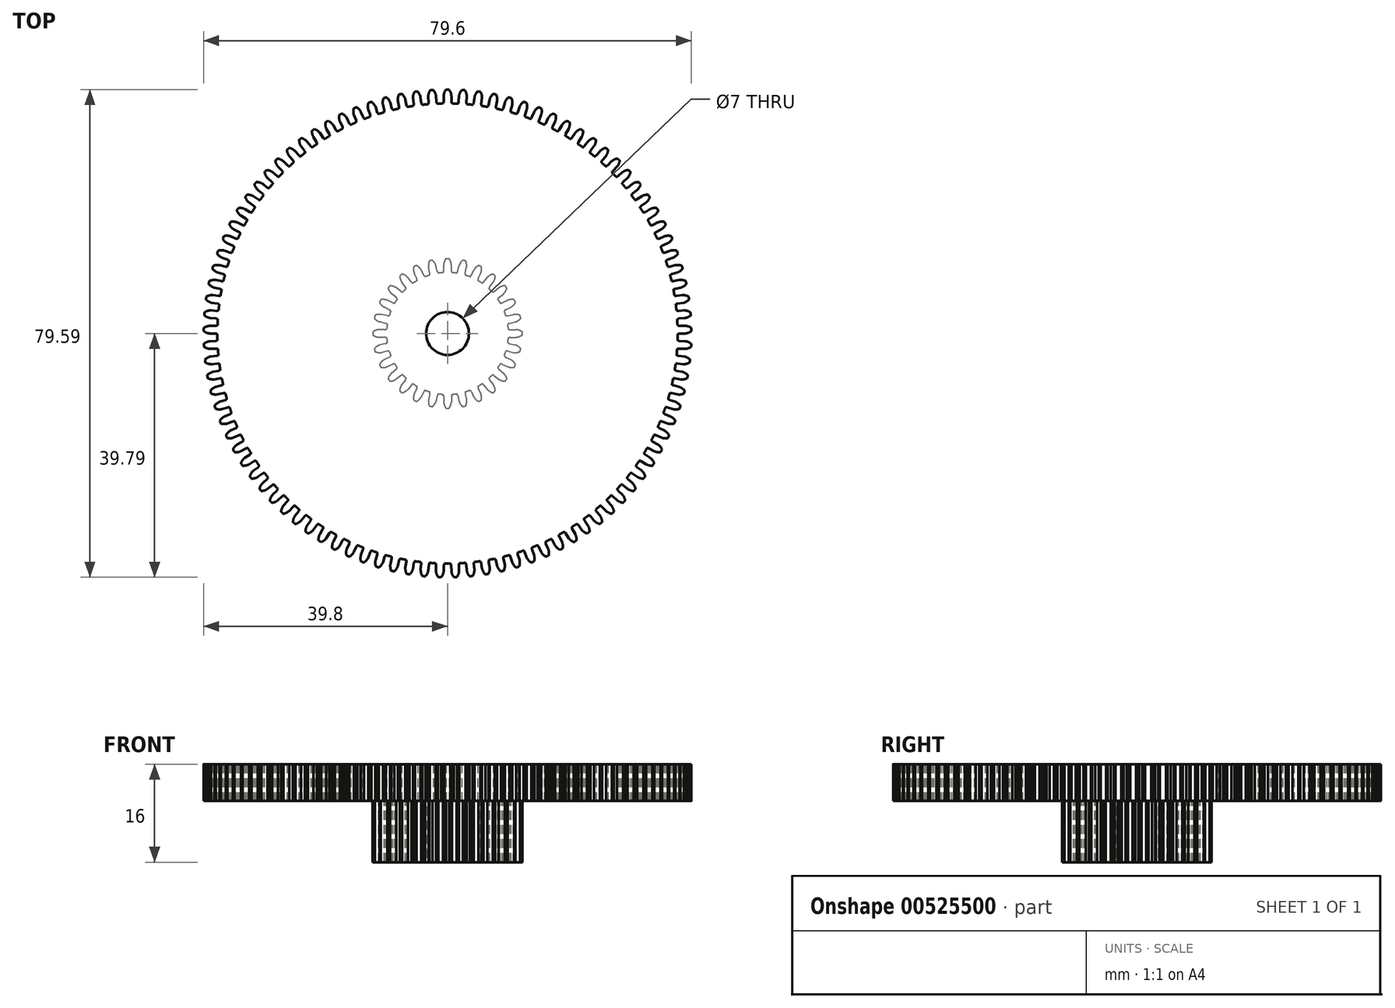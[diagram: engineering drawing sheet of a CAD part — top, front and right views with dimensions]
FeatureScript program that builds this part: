
annotation { "Feature Type Name" : "Feature", "Feature Type Description" : "" }
export const myFeature = defineFeature(function(context is Context, id is Id, definition is map)
    precondition{}
    {
        {
            var Q0;
            Q0=qCreatedBy(makeId("Top.planeOp"),FACE);
            var sketch = newSketch(context, id + "F0", { "sketchPlane" : qUnion([Q0])});
            skCircle(sketch, "E0", {"center": v(0, 0) * mm, "radius": 37.55 * mm, "construction": true});
            skCircle(sketch, "E1", {"center": v(0, 0) * mm, "radius": 38.8 * mm, "construction": true});
            skArc(sketch, "E2", {"start": v(0.25, 39.8) * mm, "mid": v(0, 39.8) * mm, "end": v(-0.25, 39.8) * mm});
            skLineSegment(sketch, "E3", {"start": v(-0.63, 39.8) * mm, "end": v(-0.63, 37.54) * mm, "construction": true});
            skLineSegment(sketch, "E4", {"start": v(0.63, 37.54) * mm, "end": v(0.63, 39.8) * mm, "construction": true});
            skArc(sketch, "E5", {"start": v(-0.25, 39.8) * mm, "mid": v(-0.5, 39.32) * mm, "end": v(-0.63, 38.8) * mm});
            skArc(sketch, "E6", {"start": v(-0.73, 37.54) * mm, "mid": v(-0.67, 37.69) * mm, "end": v(-0.63, 37.84) * mm});
            skLineSegment(sketch, "E7", {"start": v(-0.63, 37.84) * mm, "end": v(-0.63, 38.8) * mm});
            skArc(sketch, "E8.MirrorCS", {"start": v(0.25, 39.8) * mm, "mid": v(0.5, 39.32) * mm, "end": v(0.63, 38.8) * mm});
            skLineSegment(sketch, "E9.MirrorCS", {"start": v(0.63, 37.84) * mm, "end": v(0.63, 38.8) * mm});
            skArc(sketch, "E10.MirrorCS", {"start": v(0.73, 37.54) * mm, "mid": v(0.67, 37.69) * mm, "end": v(0.63, 37.84) * mm});
            skArc(sketch, "E11.1.0", {"start": v(-3.16, 37.42) * mm, "mid": v(-3.1, 37.57) * mm, "end": v(-3.08, 37.72) * mm});
            skLineSegment(sketch, "E11.1.1", {"start": v(-3.08, 37.72) * mm, "end": v(-3.14, 38.67) * mm});
            skArc(sketch, "E11.1.2", {"start": v(-2.83, 39.7) * mm, "mid": v(-3.05, 39.2) * mm, "end": v(-3.14, 38.67) * mm});
            skArc(sketch, "E11.1.3", {"start": v(-2.33, 39.73) * mm, "mid": v(-2.58, 39.72) * mm, "end": v(-2.83, 39.7) * mm});
            skArc(sketch, "E11.1.4", {"start": v(-2.33, 39.73) * mm, "mid": v(-2.04, 39.27) * mm, "end": v(-1.88, 38.75) * mm});
            skLineSegment(sketch, "E11.1.5", {"start": v(-1.82, 37.8) * mm, "end": v(-1.88, 38.75) * mm});
            skArc(sketch, "E11.1.6", {"start": v(-1.7, 37.51) * mm, "mid": v(-1.77, 37.65) * mm, "end": v(-1.82, 37.8) * mm});
            skArc(sketch, "E11.2.0", {"start": v(-5.57, 37.13) * mm, "mid": v(-5.53, 37.29) * mm, "end": v(-5.51, 37.45) * mm});
            skLineSegment(sketch, "E11.2.1", {"start": v(-5.51, 37.45) * mm, "end": v(-5.63, 38.39) * mm});
            skArc(sketch, "E11.2.2", {"start": v(-5.39, 39.43) * mm, "mid": v(-5.58, 38.93) * mm, "end": v(-5.63, 38.39) * mm});
            skArc(sketch, "E11.2.3", {"start": v(-4.9, 39.5) * mm, "mid": v(-5.14, 39.47) * mm, "end": v(-5.39, 39.43) * mm});
            skArc(sketch, "E11.2.4", {"start": v(-4.9, 39.5) * mm, "mid": v(-4.58, 39.06) * mm, "end": v(-4.39, 38.55) * mm});
            skLineSegment(sketch, "E11.2.5", {"start": v(-4.27, 37.6) * mm, "end": v(-4.39, 38.55) * mm});
            skArc(sketch, "E11.2.6", {"start": v(-4.13, 37.32) * mm, "mid": v(-4.2, 37.46) * mm, "end": v(-4.27, 37.6) * mm});
            skArc(sketch, "E11.3.0", {"start": v(-7.96, 36.7) * mm, "mid": v(-7.93, 36.85) * mm, "end": v(-7.92, 37.01) * mm});
            skLineSegment(sketch, "E11.3.1", {"start": v(-7.92, 37.01) * mm, "end": v(-8.1, 37.94) * mm});
            skArc(sketch, "E11.3.2", {"start": v(-7.93, 39) * mm, "mid": v(-8.1, 38.48) * mm, "end": v(-8.1, 37.94) * mm});
            skArc(sketch, "E11.3.3", {"start": v(-7.44, 39.1) * mm, "mid": v(-7.69, 39.05) * mm, "end": v(-7.93, 39) * mm});
            skArc(sketch, "E11.3.4", {"start": v(-7.44, 39.1) * mm, "mid": v(-7.1, 38.68) * mm, "end": v(-6.87, 38.19) * mm});
            skLineSegment(sketch, "E11.3.5", {"start": v(-6.7, 37.25) * mm, "end": v(-6.87, 38.19) * mm});
            skArc(sketch, "E11.3.6", {"start": v(-6.54, 36.98) * mm, "mid": v(-6.62, 37.1) * mm, "end": v(-6.7, 37.25) * mm});
            skArc(sketch, "E11.4.0", {"start": v(-10.32, 36.1) * mm, "mid": v(-10.3, 36.26) * mm, "end": v(-10.3, 36.42) * mm});
            skLineSegment(sketch, "E11.4.1", {"start": v(-10.3, 36.42) * mm, "end": v(-10.55, 37.34) * mm});
            skArc(sketch, "E11.4.2", {"start": v(-10.44, 38.4) * mm, "mid": v(-10.57, 37.88) * mm, "end": v(-10.55, 37.34) * mm});
            skArc(sketch, "E11.4.3", {"start": v(-9.96, 38.53) * mm, "mid": v(-10.2, 38.47) * mm, "end": v(-10.44, 38.4) * mm});
            skArc(sketch, "E11.4.4", {"start": v(-9.96, 38.53) * mm, "mid": v(-9.58, 38.14) * mm, "end": v(-9.33, 37.66) * mm});
            skLineSegment(sketch, "E11.4.5", {"start": v(-9.09, 36.74) * mm, "end": v(-9.33, 37.66) * mm});
            skArc(sketch, "E11.4.6", {"start": v(-8.91, 36.48) * mm, "mid": v(-9.01, 36.6) * mm, "end": v(-9.09, 36.74) * mm});
            skArc(sketch, "E11.5.0", {"start": v(-12.64, 35.36) * mm, "mid": v(-12.63, 35.52) * mm, "end": v(-12.64, 35.68) * mm});
            skLineSegment(sketch, "E11.5.1", {"start": v(-12.64, 35.68) * mm, "end": v(-12.94, 36.58) * mm});
            skArc(sketch, "E11.5.2", {"start": v(-12.9, 37.65) * mm, "mid": v(-13, 37.12) * mm, "end": v(-12.94, 36.58) * mm});
            skArc(sketch, "E11.5.3", {"start": v(-12.43, 37.8) * mm, "mid": v(-12.67, 37.73) * mm, "end": v(-12.9, 37.65) * mm});
            skArc(sketch, "E11.5.4", {"start": v(-12.43, 37.8) * mm, "mid": v(-12.03, 37.44) * mm, "end": v(-11.75, 36.98) * mm});
            skLineSegment(sketch, "E11.5.5", {"start": v(-11.45, 36.08) * mm, "end": v(-11.75, 36.98) * mm});
            skArc(sketch, "E11.5.6", {"start": v(-11.26, 35.82) * mm, "mid": v(-11.36, 35.94) * mm, "end": v(-11.45, 36.08) * mm});
            skArc(sketch, "E11.6.0", {"start": v(-14.9, 34.47) * mm, "mid": v(-14.9, 34.63) * mm, "end": v(-14.92, 34.78) * mm});
            skLineSegment(sketch, "E11.6.1", {"start": v(-14.92, 34.78) * mm, "end": v(-15.28, 35.66) * mm});
            skArc(sketch, "E11.6.2", {"start": v(-15.31, 36.74) * mm, "mid": v(-15.37, 36.2) * mm, "end": v(-15.28, 35.66) * mm});
            skArc(sketch, "E11.6.3", {"start": v(-14.85, 36.93) * mm, "mid": v(-15.08, 36.83) * mm, "end": v(-15.31, 36.74) * mm});
            skArc(sketch, "E11.6.4", {"start": v(-14.85, 36.93) * mm, "mid": v(-14.43, 36.58) * mm, "end": v(-14.12, 36.14) * mm});
            skLineSegment(sketch, "E11.6.5", {"start": v(-13.76, 35.26) * mm, "end": v(-14.12, 36.14) * mm});
            skArc(sketch, "E11.6.6", {"start": v(-13.55, 35.02) * mm, "mid": v(-13.67, 35.13) * mm, "end": v(-13.76, 35.26) * mm});
            skArc(sketch, "E11.7.0", {"start": v(-17.1, 33.43) * mm, "mid": v(-17.1, 33.59) * mm, "end": v(-17.14, 33.75) * mm});
            skLineSegment(sketch, "E11.7.1", {"start": v(-17.14, 33.75) * mm, "end": v(-17.56, 34.6) * mm});
            skArc(sketch, "E11.7.2", {"start": v(-17.66, 35.67) * mm, "mid": v(-17.68, 35.13) * mm, "end": v(-17.56, 34.6) * mm});
            skArc(sketch, "E11.7.3", {"start": v(-17.2, 35.89) * mm, "mid": v(-17.43, 35.78) * mm, "end": v(-17.66, 35.67) * mm});
            skArc(sketch, "E11.7.4", {"start": v(-17.2, 35.89) * mm, "mid": v(-16.77, 35.57) * mm, "end": v(-16.43, 35.15) * mm});
            skLineSegment(sketch, "E11.7.5", {"start": v(-16.01, 34.3) * mm, "end": v(-16.43, 35.15) * mm});
            skArc(sketch, "E11.7.6", {"start": v(-15.8, 34.07) * mm, "mid": v(-15.91, 34.17) * mm, "end": v(-16.01, 34.3) * mm});
            skArc(sketch, "E11.8.0", {"start": v(-19.23, 32.25) * mm, "mid": v(-19.25, 32.41) * mm, "end": v(-19.3, 32.56) * mm});
            skLineSegment(sketch, "E11.8.1", {"start": v(-19.3, 32.56) * mm, "end": v(-19.76, 33.4) * mm});
            skArc(sketch, "E11.8.2", {"start": v(-19.93, 34.45) * mm, "mid": v(-19.92, 33.9) * mm, "end": v(-19.76, 33.4) * mm});
            skArc(sketch, "E11.8.3", {"start": v(-19.5, 34.7) * mm, "mid": v(-19.71, 34.57) * mm, "end": v(-19.93, 34.45) * mm});
            skArc(sketch, "E11.8.4", {"start": v(-19.5, 34.7) * mm, "mid": v(-19.04, 34.41) * mm, "end": v(-18.67, 34.01) * mm});
            skLineSegment(sketch, "E11.8.5", {"start": v(-18.2, 33.19) * mm, "end": v(-18.67, 34.01) * mm});
            skArc(sketch, "E11.8.6", {"start": v(-17.96, 32.97) * mm, "mid": v(-18.09, 33.07) * mm, "end": v(-18.2, 33.19) * mm});
            skArc(sketch, "E11.9.0", {"start": v(-21.28, 30.94) * mm, "mid": v(-21.3, 31.1) * mm, "end": v(-21.36, 31.25) * mm});
            skLineSegment(sketch, "E11.9.1", {"start": v(-21.36, 31.25) * mm, "end": v(-21.88, 32.04) * mm});
            skArc(sketch, "E11.9.2", {"start": v(-22.12, 33.09) * mm, "mid": v(-22.07, 32.55) * mm, "end": v(-21.88, 32.04) * mm});
            skArc(sketch, "E11.9.3", {"start": v(-21.7, 33.36) * mm, "mid": v(-21.91, 33.23) * mm, "end": v(-22.12, 33.09) * mm});
            skArc(sketch, "E11.9.4", {"start": v(-21.7, 33.36) * mm, "mid": v(-21.22, 33.1) * mm, "end": v(-20.83, 32.73) * mm});
            skLineSegment(sketch, "E11.9.5", {"start": v(-20.3, 31.94) * mm, "end": v(-20.83, 32.73) * mm});
            skArc(sketch, "E11.9.6", {"start": v(-20.06, 31.74) * mm, "mid": v(-20.2, 31.83) * mm, "end": v(-20.3, 31.94) * mm});
            skArc(sketch, "E11.10.0", {"start": v(-23.23, 29.5) * mm, "mid": v(-23.27, 29.65) * mm, "end": v(-23.34, 29.8) * mm});
            skLineSegment(sketch, "E11.10.1", {"start": v(-23.34, 29.8) * mm, "end": v(-23.9, 30.56) * mm});
            skArc(sketch, "E11.10.2", {"start": v(-24.21, 31.59) * mm, "mid": v(-24.13, 31.05) * mm, "end": v(-23.9, 30.56) * mm});
            skArc(sketch, "E11.10.3", {"start": v(-23.82, 31.89) * mm, "mid": v(-24.02, 31.74) * mm, "end": v(-24.21, 31.59) * mm});
            skArc(sketch, "E11.10.4", {"start": v(-23.82, 31.89) * mm, "mid": v(-23.32, 31.66) * mm, "end": v(-22.9, 31.32) * mm});
            skLineSegment(sketch, "E11.10.5", {"start": v(-22.33, 30.56) * mm, "end": v(-22.9, 31.32) * mm});
            skArc(sketch, "E11.10.6", {"start": v(-22.07, 30.38) * mm, "mid": v(-22.21, 30.46) * mm, "end": v(-22.33, 30.56) * mm});
            skArc(sketch, "E11.11.0", {"start": v(-25.1, 27.93) * mm, "mid": v(-25.14, 28.08) * mm, "end": v(-25.22, 28.23) * mm});
            skLineSegment(sketch, "E11.11.1", {"start": v(-25.22, 28.23) * mm, "end": v(-25.84, 28.95) * mm});
            skArc(sketch, "E11.11.2", {"start": v(-26.2, 29.95) * mm, "mid": v(-26.1, 29.42) * mm, "end": v(-25.84, 28.95) * mm});
            skArc(sketch, "E11.11.3", {"start": v(-25.83, 30.28) * mm, "mid": v(-26.02, 30.12) * mm, "end": v(-26.2, 29.95) * mm});
            skArc(sketch, "E11.11.4", {"start": v(-25.83, 30.28) * mm, "mid": v(-25.32, 30.09) * mm, "end": v(-24.89, 29.77) * mm});
            skLineSegment(sketch, "E11.11.5", {"start": v(-24.27, 29.05) * mm, "end": v(-24.89, 29.77) * mm});
            skArc(sketch, "E11.11.6", {"start": v(-24, 28.89) * mm, "mid": v(-24.14, 28.96) * mm, "end": v(-24.27, 29.05) * mm});
            skArc(sketch, "E11.12.0", {"start": v(-26.85, 26.25) * mm, "mid": v(-26.9, 26.4) * mm, "end": v(-27, 26.54) * mm});
            skLineSegment(sketch, "E11.12.1", {"start": v(-27, 26.54) * mm, "end": v(-27.66, 27.21) * mm});
            skArc(sketch, "E11.12.2", {"start": v(-28.1, 28.2) * mm, "mid": v(-27.94, 27.67) * mm, "end": v(-27.66, 27.21) * mm});
            skArc(sketch, "E11.12.3", {"start": v(-27.74, 28.54) * mm, "mid": v(-27.91, 28.37) * mm, "end": v(-28.1, 28.2) * mm});
            skArc(sketch, "E11.12.4", {"start": v(-27.74, 28.54) * mm, "mid": v(-27.22, 28.39) * mm, "end": v(-26.76, 28.1) * mm});
            skLineSegment(sketch, "E11.12.5", {"start": v(-26.1, 27.42) * mm, "end": v(-26.76, 28.1) * mm});
            skArc(sketch, "E11.12.6", {"start": v(-25.81, 27.27) * mm, "mid": v(-25.96, 27.33) * mm, "end": v(-26.1, 27.42) * mm});
            skArc(sketch, "E11.13.0", {"start": v(-28.5, 24.46) * mm, "mid": v(-28.56, 24.6) * mm, "end": v(-28.65, 24.73) * mm});
            skLineSegment(sketch, "E11.13.1", {"start": v(-28.65, 24.73) * mm, "end": v(-29.36, 25.37) * mm});
            skArc(sketch, "E11.13.2", {"start": v(-29.86, 26.32) * mm, "mid": v(-29.67, 25.8) * mm, "end": v(-29.36, 25.37) * mm});
            skArc(sketch, "E11.13.3", {"start": v(-29.52, 26.69) * mm, "mid": v(-29.7, 26.5) * mm, "end": v(-29.86, 26.32) * mm});
            skArc(sketch, "E11.13.4", {"start": v(-29.52, 26.69) * mm, "mid": v(-29, 26.56) * mm, "end": v(-28.52, 26.3) * mm});
            skLineSegment(sketch, "E11.13.5", {"start": v(-27.81, 25.67) * mm, "end": v(-28.52, 26.3) * mm});
            skArc(sketch, "E11.13.6", {"start": v(-27.52, 25.54) * mm, "mid": v(-27.67, 25.6) * mm, "end": v(-27.81, 25.67) * mm});
            skArc(sketch, "E11.14.0", {"start": v(-30.02, 22.56) * mm, "mid": v(-30.1, 22.7) * mm, "end": v(-30.2, 22.83) * mm});
            skLineSegment(sketch, "E11.14.1", {"start": v(-30.2, 22.83) * mm, "end": v(-30.94, 23.41) * mm});
            skArc(sketch, "E11.14.2", {"start": v(-31.5, 24.33) * mm, "mid": v(-31.28, 23.83) * mm, "end": v(-30.94, 23.41) * mm});
            skArc(sketch, "E11.14.3", {"start": v(-31.2, 24.72) * mm, "mid": v(-31.35, 24.53) * mm, "end": v(-31.5, 24.33) * mm});
            skArc(sketch, "E11.14.4", {"start": v(-31.2, 24.72) * mm, "mid": v(-30.66, 24.63) * mm, "end": v(-30.17, 24.4) * mm});
            skLineSegment(sketch, "E11.14.5", {"start": v(-29.42, 23.82) * mm, "end": v(-30.17, 24.4) * mm});
            skArc(sketch, "E11.14.6", {"start": v(-29.12, 23.7) * mm, "mid": v(-29.27, 23.75) * mm, "end": v(-29.42, 23.82) * mm});
            skArc(sketch, "E11.15.0", {"start": v(-31.41, 20.57) * mm, "mid": v(-31.5, 20.7) * mm, "end": v(-31.6, 20.82) * mm});
            skLineSegment(sketch, "E11.15.1", {"start": v(-31.6, 20.82) * mm, "end": v(-32.4, 21.36) * mm});
            skArc(sketch, "E11.15.2", {"start": v(-33, 22.24) * mm, "mid": v(-32.76, 21.76) * mm, "end": v(-32.4, 21.36) * mm});
            skArc(sketch, "E11.15.3", {"start": v(-32.73, 22.65) * mm, "mid": v(-32.87, 22.45) * mm, "end": v(-33, 22.24) * mm});
            skArc(sketch, "E11.15.4", {"start": v(-32.73, 22.65) * mm, "mid": v(-32.19, 22.6) * mm, "end": v(-31.68, 22.4) * mm});
            skLineSegment(sketch, "E11.15.5", {"start": v(-30.9, 21.86) * mm, "end": v(-31.68, 22.4) * mm});
            skArc(sketch, "E11.15.6", {"start": v(-30.6, 21.77) * mm, "mid": v(-30.75, 21.8) * mm, "end": v(-30.9, 21.86) * mm});
            skArc(sketch, "E11.16.0", {"start": v(-32.68, 18.5) * mm, "mid": v(-32.77, 18.62) * mm, "end": v(-32.89, 18.73) * mm});
            skLineSegment(sketch, "E11.16.1", {"start": v(-32.89, 18.73) * mm, "end": v(-33.7, 19.22) * mm});
            skArc(sketch, "E11.16.2", {"start": v(-34.38, 20.06) * mm, "mid": v(-34.1, 19.6) * mm, "end": v(-33.7, 19.22) * mm});
            skArc(sketch, "E11.16.3", {"start": v(-34.12, 20.49) * mm, "mid": v(-34.25, 20.27) * mm, "end": v(-34.38, 20.06) * mm});
            skArc(sketch, "E11.16.4", {"start": v(-34.12, 20.49) * mm, "mid": v(-33.58, 20.46) * mm, "end": v(-33.07, 20.3) * mm});
            skLineSegment(sketch, "E11.16.5", {"start": v(-32.25, 19.82) * mm, "end": v(-33.07, 20.3) * mm});
            skArc(sketch, "E11.16.6", {"start": v(-31.94, 19.75) * mm, "mid": v(-32.1, 19.77) * mm, "end": v(-32.25, 19.82) * mm});
            skArc(sketch, "E11.17.0", {"start": v(-33.8, 16.34) * mm, "mid": v(-33.91, 16.46) * mm, "end": v(-34.03, 16.57) * mm});
            skLineSegment(sketch, "E11.17.1", {"start": v(-34.03, 16.57) * mm, "end": v(-34.88, 17) * mm});
            skArc(sketch, "E11.17.2", {"start": v(-35.6, 17.79) * mm, "mid": v(-35.3, 17.34) * mm, "end": v(-34.88, 17) * mm});
            skArc(sketch, "E11.17.3", {"start": v(-35.38, 18.23) * mm, "mid": v(-35.5, 18.01) * mm, "end": v(-35.6, 17.79) * mm});
            skArc(sketch, "E11.17.4", {"start": v(-35.38, 18.23) * mm, "mid": v(-34.84, 18.25) * mm, "end": v(-34.31, 18.12) * mm});
            skLineSegment(sketch, "E11.17.5", {"start": v(-33.46, 17.69) * mm, "end": v(-34.31, 18.12) * mm});
            skArc(sketch, "E11.17.6", {"start": v(-33.15, 17.64) * mm, "mid": v(-33.3, 17.65) * mm, "end": v(-33.46, 17.69) * mm});
            skArc(sketch, "E11.18.0", {"start": v(-34.8, 14.12) * mm, "mid": v(-34.9, 14.23) * mm, "end": v(-35.03, 14.33) * mm});
            skLineSegment(sketch, "E11.18.1", {"start": v(-35.03, 14.33) * mm, "end": v(-35.9, 14.7) * mm});
            skArc(sketch, "E11.18.2", {"start": v(-36.68, 15.45) * mm, "mid": v(-36.34, 15.02) * mm, "end": v(-35.9, 14.7) * mm});
            skArc(sketch, "E11.18.3", {"start": v(-36.48, 15.9) * mm, "mid": v(-36.58, 15.68) * mm, "end": v(-36.68, 15.45) * mm});
            skArc(sketch, "E11.18.4", {"start": v(-36.48, 15.9) * mm, "mid": v(-35.94, 15.96) * mm, "end": v(-35.41, 15.86) * mm});
            skLineSegment(sketch, "E11.18.5", {"start": v(-34.54, 15.48) * mm, "end": v(-35.41, 15.86) * mm});
            skArc(sketch, "E11.18.6", {"start": v(-34.22, 15.46) * mm, "mid": v(-34.38, 15.46) * mm, "end": v(-34.54, 15.48) * mm});
            skArc(sketch, "E11.19.0", {"start": v(-35.64, 11.84) * mm, "mid": v(-35.75, 11.94) * mm, "end": v(-35.89, 12.03) * mm});
            skLineSegment(sketch, "E11.19.1", {"start": v(-35.89, 12.03) * mm, "end": v(-36.78, 12.35) * mm});
            skArc(sketch, "E11.19.2", {"start": v(-37.6, 13.04) * mm, "mid": v(-37.24, 12.64) * mm, "end": v(-36.78, 12.35) * mm});
            skArc(sketch, "E11.19.3", {"start": v(-37.44, 13.51) * mm, "mid": v(-37.52, 13.28) * mm, "end": v(-37.6, 13.04) * mm});
            skArc(sketch, "E11.19.4", {"start": v(-37.44, 13.51) * mm, "mid": v(-36.9, 13.6) * mm, "end": v(-36.36, 13.53) * mm});
            skLineSegment(sketch, "E11.19.5", {"start": v(-35.47, 13.22) * mm, "end": v(-36.36, 13.53) * mm});
            skArc(sketch, "E11.19.6", {"start": v(-35.15, 13.2) * mm, "mid": v(-35.3, 13.2) * mm, "end": v(-35.47, 13.22) * mm});
            skArc(sketch, "E11.20.0", {"start": v(-36.33, 9.5) * mm, "mid": v(-36.45, 9.6) * mm, "end": v(-36.6, 9.68) * mm});
            skLineSegment(sketch, "E11.20.1", {"start": v(-36.6, 9.68) * mm, "end": v(-37.5, 9.94) * mm});
            skArc(sketch, "E11.20.2", {"start": v(-38.37, 10.58) * mm, "mid": v(-37.98, 10.2) * mm, "end": v(-37.5, 9.94) * mm});
            skArc(sketch, "E11.20.3", {"start": v(-38.23, 11.06) * mm, "mid": v(-38.3, 10.82) * mm, "end": v(-38.37, 10.58) * mm});
            skArc(sketch, "E11.20.4", {"start": v(-38.23, 11.06) * mm, "mid": v(-37.7, 11.18) * mm, "end": v(-37.16, 11.15) * mm});
            skLineSegment(sketch, "E11.20.5", {"start": v(-36.25, 10.9) * mm, "end": v(-37.16, 11.15) * mm});
            skArc(sketch, "E11.20.6", {"start": v(-35.93, 10.9) * mm, "mid": v(-36.09, 10.89) * mm, "end": v(-36.25, 10.9) * mm});
            skArc(sketch, "E11.21.0", {"start": v(-36.87, 7.13) * mm, "mid": v(-37, 7.22) * mm, "end": v(-37.14, 7.3) * mm});
            skLineSegment(sketch, "E11.21.1", {"start": v(-37.14, 7.3) * mm, "end": v(-38.07, 7.5) * mm});
            skArc(sketch, "E11.21.2", {"start": v(-38.97, 8.07) * mm, "mid": v(-38.56, 7.72) * mm, "end": v(-38.07, 7.5) * mm});
            skArc(sketch, "E11.21.3", {"start": v(-38.87, 8.56) * mm, "mid": v(-38.92, 8.32) * mm, "end": v(-38.97, 8.07) * mm});
            skArc(sketch, "E11.21.4", {"start": v(-38.87, 8.56) * mm, "mid": v(-38.35, 8.71) * mm, "end": v(-37.8, 8.72) * mm});
            skLineSegment(sketch, "E11.21.5", {"start": v(-36.88, 8.52) * mm, "end": v(-37.8, 8.72) * mm});
            skArc(sketch, "E11.21.6", {"start": v(-36.56, 8.56) * mm, "mid": v(-36.72, 8.53) * mm, "end": v(-36.88, 8.52) * mm});
            skArc(sketch, "E11.22.0", {"start": v(-37.25, 4.73) * mm, "mid": v(-37.39, 4.81) * mm, "end": v(-37.53, 4.87) * mm});
            skLineSegment(sketch, "E11.22.1", {"start": v(-37.53, 4.87) * mm, "end": v(-38.47, 5.01) * mm});
            skArc(sketch, "E11.22.2", {"start": v(-39.41, 5.53) * mm, "mid": v(-38.98, 5.2) * mm, "end": v(-38.47, 5.01) * mm});
            skArc(sketch, "E11.22.3", {"start": v(-39.34, 6.03) * mm, "mid": v(-39.38, 5.78) * mm, "end": v(-39.41, 5.53) * mm});
            skArc(sketch, "E11.22.4", {"start": v(-39.34, 6.03) * mm, "mid": v(-38.83, 6.21) * mm, "end": v(-38.3, 6.26) * mm});
            skLineSegment(sketch, "E11.22.5", {"start": v(-37.35, 6.12) * mm, "end": v(-38.3, 6.26) * mm});
            skArc(sketch, "E11.22.6", {"start": v(-37.04, 6.17) * mm, "mid": v(-37.2, 6.13) * mm, "end": v(-37.35, 6.12) * mm});
            skArc(sketch, "E11.23.0", {"start": v(-37.48, 2.31) * mm, "mid": v(-37.62, 2.38) * mm, "end": v(-37.77, 2.43) * mm});
            skLineSegment(sketch, "E11.23.1", {"start": v(-37.77, 2.43) * mm, "end": v(-38.72, 2.51) * mm});
            skArc(sketch, "E11.23.2", {"start": v(-39.69, 2.97) * mm, "mid": v(-39.24, 2.67) * mm, "end": v(-38.72, 2.51) * mm});
            skArc(sketch, "E11.23.3", {"start": v(-39.65, 3.47) * mm, "mid": v(-39.67, 3.22) * mm, "end": v(-39.69, 2.97) * mm});
            skArc(sketch, "E11.23.4", {"start": v(-39.65, 3.47) * mm, "mid": v(-39.15, 3.69) * mm, "end": v(-38.62, 3.76) * mm});
            skLineSegment(sketch, "E11.23.5", {"start": v(-37.67, 3.69) * mm, "end": v(-38.62, 3.76) * mm});
            skArc(sketch, "E11.23.6", {"start": v(-37.36, 3.76) * mm, "mid": v(-37.51, 3.71) * mm, "end": v(-37.67, 3.69) * mm});
            skArc(sketch, "E11.24.0", {"start": v(-37.55, -0.12) * mm, "mid": v(-37.7, -0.06) * mm, "end": v(-37.85, -0.02) * mm});
            skLineSegment(sketch, "E11.24.1", {"start": v(-37.85, -0.02) * mm, "end": v(-38.8, 0) * mm});
            skArc(sketch, "E11.24.2", {"start": v(-39.8, 0.4) * mm, "mid": v(-39.33, 0.13) * mm, "end": v(-38.8, 0) * mm});
            skArc(sketch, "E11.24.3", {"start": v(-39.79, 0.9) * mm, "mid": v(-39.8, 0.64) * mm, "end": v(-39.8, 0.4) * mm});
            skArc(sketch, "E11.24.4", {"start": v(-39.79, 0.9) * mm, "mid": v(-39.3, 1.14) * mm, "end": v(-38.78, 1.26) * mm});
            skLineSegment(sketch, "E11.24.5", {"start": v(-37.83, 1.24) * mm, "end": v(-38.78, 1.26) * mm});
            skArc(sketch, "E11.24.6", {"start": v(-37.53, 1.34) * mm, "mid": v(-37.67, 1.28) * mm, "end": v(-37.83, 1.24) * mm});
            skArc(sketch, "E11.25.0", {"start": v(-37.46, -2.55) * mm, "mid": v(-37.61, -2.5) * mm, "end": v(-37.77, -2.47) * mm});
            skLineSegment(sketch, "E11.25.1", {"start": v(-37.77, -2.47) * mm, "end": v(-38.72, -2.51) * mm});
            skArc(sketch, "E11.25.2", {"start": v(-39.74, -2.18) * mm, "mid": v(-39.25, -2.42) * mm, "end": v(-38.72, -2.51) * mm});
            skArc(sketch, "E11.25.3", {"start": v(-39.76, -1.68) * mm, "mid": v(-39.75, -1.93) * mm, "end": v(-39.74, -2.18) * mm});
            skArc(sketch, "E11.25.4", {"start": v(-39.76, -1.68) * mm, "mid": v(-39.3, -1.4) * mm, "end": v(-38.78, -1.26) * mm});
            skLineSegment(sketch, "E11.25.5", {"start": v(-37.83, -1.21) * mm, "end": v(-38.78, -1.26) * mm});
            skArc(sketch, "E11.25.6", {"start": v(-37.53, -1.1) * mm, "mid": v(-37.68, -1.16) * mm, "end": v(-37.83, -1.21) * mm});
            skArc(sketch, "E11.26.0", {"start": v(-37.22, -4.97) * mm, "mid": v(-37.37, -4.93) * mm, "end": v(-37.53, -4.9) * mm});
            skLineSegment(sketch, "E11.26.1", {"start": v(-37.53, -4.9) * mm, "end": v(-38.47, -5.01) * mm});
            skArc(sketch, "E11.26.2", {"start": v(-39.52, -4.75) * mm, "mid": v(-39.01, -4.95) * mm, "end": v(-38.47, -5.01) * mm});
            skArc(sketch, "E11.26.3", {"start": v(-39.57, -4.25) * mm, "mid": v(-39.54, -4.5) * mm, "end": v(-39.52, -4.75) * mm});
            skArc(sketch, "E11.26.4", {"start": v(-39.57, -4.25) * mm, "mid": v(-39.13, -3.94) * mm, "end": v(-38.62, -3.76) * mm});
            skLineSegment(sketch, "E11.26.5", {"start": v(-37.67, -3.66) * mm, "end": v(-38.62, -3.76) * mm});
            skArc(sketch, "E11.26.6", {"start": v(-37.38, -3.52) * mm, "mid": v(-37.52, -3.6) * mm, "end": v(-37.67, -3.66) * mm});
            skArc(sketch, "E11.27.0", {"start": v(-36.82, -7.37) * mm, "mid": v(-36.98, -7.33) * mm, "end": v(-37.13, -7.32) * mm});
            skLineSegment(sketch, "E11.27.1", {"start": v(-37.13, -7.32) * mm, "end": v(-38.07, -7.5) * mm});
            skArc(sketch, "E11.27.2", {"start": v(-39.13, -7.3) * mm, "mid": v(-38.61, -7.47) * mm, "end": v(-38.07, -7.5) * mm});
            skArc(sketch, "E11.27.3", {"start": v(-39.21, -6.8) * mm, "mid": v(-39.17, -7.05) * mm, "end": v(-39.13, -7.3) * mm});
            skArc(sketch, "E11.27.4", {"start": v(-39.21, -6.8) * mm, "mid": v(-38.8, -6.47) * mm, "end": v(-38.3, -6.26) * mm});
            skLineSegment(sketch, "E11.27.5", {"start": v(-37.36, -6.09) * mm, "end": v(-38.3, -6.26) * mm});
            skArc(sketch, "E11.27.6", {"start": v(-37.08, -5.94) * mm, "mid": v(-37.21, -6.02) * mm, "end": v(-37.36, -6.09) * mm});
            skArc(sketch, "E11.28.0", {"start": v(-36.27, -9.74) * mm, "mid": v(-36.42, -9.71) * mm, "end": v(-36.58, -9.71) * mm});
            skLineSegment(sketch, "E11.28.1", {"start": v(-36.58, -9.71) * mm, "end": v(-37.5, -9.94) * mm});
            skArc(sketch, "E11.28.2", {"start": v(-38.57, -9.82) * mm, "mid": v(-38.05, -9.95) * mm, "end": v(-37.5, -9.94) * mm});
            skArc(sketch, "E11.28.3", {"start": v(-38.7, -9.33) * mm, "mid": v(-38.63, -9.57) * mm, "end": v(-38.57, -9.82) * mm});
            skArc(sketch, "E11.28.4", {"start": v(-38.7, -9.33) * mm, "mid": v(-38.3, -8.97) * mm, "end": v(-37.8, -8.72) * mm});
            skLineSegment(sketch, "E11.28.5", {"start": v(-36.88, -8.5) * mm, "end": v(-37.8, -8.72) * mm});
            skArc(sketch, "E11.28.6", {"start": v(-36.62, -8.32) * mm, "mid": v(-36.74, -8.42) * mm, "end": v(-36.88, -8.5) * mm});
            skArc(sketch, "E11.29.0", {"start": v(-35.56, -12.06) * mm, "mid": v(-35.72, -12.05) * mm, "end": v(-35.88, -12.06) * mm});
            skLineSegment(sketch, "E11.29.1", {"start": v(-35.88, -12.06) * mm, "end": v(-36.78, -12.35) * mm});
            skArc(sketch, "E11.29.2", {"start": v(-37.85, -12.3) * mm, "mid": v(-37.32, -12.4) * mm, "end": v(-36.78, -12.35) * mm});
            skArc(sketch, "E11.29.3", {"start": v(-38, -11.81) * mm, "mid": v(-37.93, -12.05) * mm, "end": v(-37.85, -12.3) * mm});
            skArc(sketch, "E11.29.4", {"start": v(-38, -11.81) * mm, "mid": v(-37.63, -11.43) * mm, "end": v(-37.16, -11.15) * mm});
            skLineSegment(sketch, "E11.29.5", {"start": v(-36.26, -10.86) * mm, "end": v(-37.16, -11.15) * mm});
            skArc(sketch, "E11.29.6", {"start": v(-36, -10.68) * mm, "mid": v(-36.12, -10.78) * mm, "end": v(-36.26, -10.86) * mm});
            skArc(sketch, "E11.30.0", {"start": v(-34.7, -14.34) * mm, "mid": v(-34.86, -14.34) * mm, "end": v(-35.02, -14.36) * mm});
            skLineSegment(sketch, "E11.30.1", {"start": v(-35.02, -14.36) * mm, "end": v(-35.9, -14.7) * mm});
            skArc(sketch, "E11.30.2", {"start": v(-36.98, -14.72) * mm, "mid": v(-36.44, -14.78) * mm, "end": v(-35.9, -14.7) * mm});
            skArc(sketch, "E11.30.3", {"start": v(-37.16, -14.25) * mm, "mid": v(-37.07, -14.48) * mm, "end": v(-36.98, -14.72) * mm});
            skArc(sketch, "E11.30.4", {"start": v(-37.16, -14.25) * mm, "mid": v(-36.81, -13.84) * mm, "end": v(-36.36, -13.53) * mm});
            skLineSegment(sketch, "E11.30.5", {"start": v(-35.48, -13.19) * mm, "end": v(-36.36, -13.53) * mm});
            skArc(sketch, "E11.30.6", {"start": v(-35.23, -12.98) * mm, "mid": v(-35.35, -13.1) * mm, "end": v(-35.48, -13.19) * mm});
            skArc(sketch, "E11.31.0", {"start": v(-33.7, -16.56) * mm, "mid": v(-33.86, -16.56) * mm, "end": v(-34.02, -16.6) * mm});
            skLineSegment(sketch, "E11.31.1", {"start": v(-34.02, -16.6) * mm, "end": v(-34.88, -17) * mm});
            skArc(sketch, "E11.31.2", {"start": v(-35.95, -17.08) * mm, "mid": v(-35.4, -17.11) * mm, "end": v(-34.88, -17) * mm});
            skArc(sketch, "E11.31.3", {"start": v(-36.16, -16.63) * mm, "mid": v(-36.06, -16.85) * mm, "end": v(-35.95, -17.08) * mm});
            skArc(sketch, "E11.31.4", {"start": v(-36.16, -16.63) * mm, "mid": v(-35.84, -16.2) * mm, "end": v(-35.41, -15.86) * mm});
            skLineSegment(sketch, "E11.31.5", {"start": v(-34.55, -15.46) * mm, "end": v(-35.41, -15.86) * mm});
            skArc(sketch, "E11.31.6", {"start": v(-34.32, -15.24) * mm, "mid": v(-34.43, -15.36) * mm, "end": v(-34.55, -15.46) * mm});
            skArc(sketch, "E11.32.0", {"start": v(-32.56, -18.7) * mm, "mid": v(-32.72, -18.72) * mm, "end": v(-32.87, -18.76) * mm});
            skLineSegment(sketch, "E11.32.1", {"start": v(-32.87, -18.76) * mm, "end": v(-33.7, -19.22) * mm});
            skArc(sketch, "E11.32.2", {"start": v(-34.77, -19.37) * mm, "mid": v(-34.23, -19.37) * mm, "end": v(-33.7, -19.22) * mm});
            skArc(sketch, "E11.32.3", {"start": v(-35, -18.93) * mm, "mid": v(-34.89, -19.15) * mm, "end": v(-34.77, -19.37) * mm});
            skArc(sketch, "E11.32.4", {"start": v(-35, -18.93) * mm, "mid": v(-34.72, -18.48) * mm, "end": v(-34.31, -18.12) * mm});
            skLineSegment(sketch, "E11.32.5", {"start": v(-33.48, -17.66) * mm, "end": v(-34.31, -18.12) * mm});
            skArc(sketch, "E11.32.6", {"start": v(-33.26, -17.43) * mm, "mid": v(-33.36, -17.55) * mm, "end": v(-33.48, -17.66) * mm});
            skArc(sketch, "E11.33.0", {"start": v(-31.28, -20.77) * mm, "mid": v(-31.44, -20.8) * mm, "end": v(-31.59, -20.85) * mm});
            skLineSegment(sketch, "E11.33.1", {"start": v(-31.59, -20.85) * mm, "end": v(-32.4, -21.36) * mm});
            skArc(sketch, "E11.33.2", {"start": v(-33.44, -21.58) * mm, "mid": v(-32.9, -21.54) * mm, "end": v(-32.4, -21.36) * mm});
            skArc(sketch, "E11.33.3", {"start": v(-33.71, -21.16) * mm, "mid": v(-33.58, -21.37) * mm, "end": v(-33.44, -21.58) * mm});
            skArc(sketch, "E11.33.4", {"start": v(-33.71, -21.16) * mm, "mid": v(-33.45, -20.68) * mm, "end": v(-33.07, -20.3) * mm});
            skLineSegment(sketch, "E11.33.5", {"start": v(-32.26, -19.79) * mm, "end": v(-33.07, -20.3) * mm});
            skArc(sketch, "E11.33.6", {"start": v(-32.06, -19.54) * mm, "mid": v(-32.15, -19.67) * mm, "end": v(-32.26, -19.79) * mm});
            skArc(sketch, "E11.34.0", {"start": v(-29.87, -22.75) * mm, "mid": v(-30.03, -22.79) * mm, "end": v(-30.17, -22.85) * mm});
            skLineSegment(sketch, "E11.34.1", {"start": v(-30.17, -22.85) * mm, "end": v(-30.94, -23.41) * mm});
            skArc(sketch, "E11.34.2", {"start": v(-31.97, -23.7) * mm, "mid": v(-31.44, -23.63) * mm, "end": v(-30.94, -23.41) * mm});
            skArc(sketch, "E11.34.3", {"start": v(-32.27, -23.3) * mm, "mid": v(-32.12, -23.5) * mm, "end": v(-31.97, -23.7) * mm});
            skArc(sketch, "E11.34.4", {"start": v(-32.27, -23.3) * mm, "mid": v(-32.04, -22.8) * mm, "end": v(-31.68, -22.4) * mm});
            skLineSegment(sketch, "E11.34.5", {"start": v(-30.92, -21.84) * mm, "end": v(-31.68, -22.4) * mm});
            skArc(sketch, "E11.34.6", {"start": v(-30.73, -21.58) * mm, "mid": v(-30.81, -21.71) * mm, "end": v(-30.92, -21.84) * mm});
            skArc(sketch, "E11.35.0", {"start": v(-28.34, -24.64) * mm, "mid": v(-28.49, -24.69) * mm, "end": v(-28.63, -24.76) * mm});
            skLineSegment(sketch, "E11.35.1", {"start": v(-28.63, -24.76) * mm, "end": v(-29.36, -25.37) * mm});
            skArc(sketch, "E11.35.2", {"start": v(-30.37, -25.72) * mm, "mid": v(-29.84, -25.61) * mm, "end": v(-29.36, -25.37) * mm});
            skArc(sketch, "E11.35.3", {"start": v(-30.7, -25.34) * mm, "mid": v(-30.53, -25.53) * mm, "end": v(-30.37, -25.72) * mm});
            skArc(sketch, "E11.35.4", {"start": v(-30.7, -25.34) * mm, "mid": v(-30.5, -24.83) * mm, "end": v(-30.17, -24.4) * mm});
            skLineSegment(sketch, "E11.35.5", {"start": v(-29.44, -23.8) * mm, "end": v(-30.17, -24.4) * mm});
            skArc(sketch, "E11.35.6", {"start": v(-29.27, -23.52) * mm, "mid": v(-29.34, -23.66) * mm, "end": v(-29.44, -23.8) * mm});
            skArc(sketch, "E11.36.0", {"start": v(-26.68, -26.42) * mm, "mid": v(-26.83, -26.48) * mm, "end": v(-26.97, -26.56) * mm});
            skLineSegment(sketch, "E11.36.1", {"start": v(-26.97, -26.56) * mm, "end": v(-27.66, -27.21) * mm});
            skArc(sketch, "E11.36.2", {"start": v(-28.65, -27.63) * mm, "mid": v(-28.12, -27.49) * mm, "end": v(-27.66, -27.21) * mm});
            skArc(sketch, "E11.36.3", {"start": v(-28.99, -27.27) * mm, "mid": v(-28.82, -27.45) * mm, "end": v(-28.65, -27.63) * mm});
            skArc(sketch, "E11.36.4", {"start": v(-28.99, -27.27) * mm, "mid": v(-28.82, -26.75) * mm, "end": v(-28.52, -26.3) * mm});
            skLineSegment(sketch, "E11.36.5", {"start": v(-27.84, -25.65) * mm, "end": v(-28.52, -26.3) * mm});
            skArc(sketch, "E11.36.6", {"start": v(-27.69, -25.37) * mm, "mid": v(-27.75, -25.51) * mm, "end": v(-27.84, -25.65) * mm});
            skArc(sketch, "E11.37.0", {"start": v(-24.92, -28.1) * mm, "mid": v(-25.06, -28.16) * mm, "end": v(-25.2, -28.25) * mm});
            skLineSegment(sketch, "E11.37.1", {"start": v(-25.2, -28.25) * mm, "end": v(-25.84, -28.95) * mm});
            skArc(sketch, "E11.37.2", {"start": v(-26.8, -29.43) * mm, "mid": v(-26.28, -29.25) * mm, "end": v(-25.84, -28.95) * mm});
            skArc(sketch, "E11.37.3", {"start": v(-27.16, -29.09) * mm, "mid": v(-26.98, -29.26) * mm, "end": v(-26.8, -29.43) * mm});
            skArc(sketch, "E11.37.4", {"start": v(-27.16, -29.09) * mm, "mid": v(-27.03, -28.56) * mm, "end": v(-26.76, -28.1) * mm});
            skLineSegment(sketch, "E11.37.5", {"start": v(-26.12, -27.4) * mm, "end": v(-26.76, -28.1) * mm});
            skArc(sketch, "E11.37.6", {"start": v(-25.99, -27.1) * mm, "mid": v(-26.04, -27.26) * mm, "end": v(-26.12, -27.4) * mm});
            skArc(sketch, "E11.38.0", {"start": v(-23.04, -29.65) * mm, "mid": v(-23.19, -29.72) * mm, "end": v(-23.31, -29.82) * mm});
            skLineSegment(sketch, "E11.38.1", {"start": v(-23.31, -29.82) * mm, "end": v(-23.9, -30.56) * mm});
            skArc(sketch, "E11.38.2", {"start": v(-24.84, -31.1) * mm, "mid": v(-24.34, -30.9) * mm, "end": v(-23.9, -30.56) * mm});
            skArc(sketch, "E11.38.3", {"start": v(-25.22, -30.79) * mm, "mid": v(-25.03, -30.94) * mm, "end": v(-24.84, -31.1) * mm});
            skArc(sketch, "E11.38.4", {"start": v(-25.22, -30.79) * mm, "mid": v(-25.13, -30.25) * mm, "end": v(-24.89, -29.77) * mm});
            skLineSegment(sketch, "E11.38.5", {"start": v(-24.29, -29.03) * mm, "end": v(-24.89, -29.77) * mm});
            skArc(sketch, "E11.38.6", {"start": v(-24.18, -28.73) * mm, "mid": v(-24.22, -28.88) * mm, "end": v(-24.29, -29.03) * mm});
            skArc(sketch, "E11.39.0", {"start": v(-21.08, -31.08) * mm, "mid": v(-21.21, -31.16) * mm, "end": v(-21.33, -31.27) * mm});
            skLineSegment(sketch, "E11.39.1", {"start": v(-21.33, -31.27) * mm, "end": v(-21.88, -32.04) * mm});
            skArc(sketch, "E11.39.2", {"start": v(-22.77, -32.64) * mm, "mid": v(-22.28, -32.4) * mm, "end": v(-21.88, -32.04) * mm});
            skArc(sketch, "E11.39.3", {"start": v(-23.18, -32.35) * mm, "mid": v(-22.97, -32.5) * mm, "end": v(-22.77, -32.64) * mm});
            skArc(sketch, "E11.39.4", {"start": v(-23.18, -32.35) * mm, "mid": v(-23.11, -31.82) * mm, "end": v(-22.9, -31.32) * mm});
            skLineSegment(sketch, "E11.39.5", {"start": v(-22.36, -30.54) * mm, "end": v(-22.9, -31.32) * mm});
            skArc(sketch, "E11.39.6", {"start": v(-22.27, -30.24) * mm, "mid": v(-22.3, -30.4) * mm, "end": v(-22.36, -30.54) * mm});
            skArc(sketch, "E11.40.0", {"start": v(-19.02, -32.38) * mm, "mid": v(-19.15, -32.47) * mm, "end": v(-19.26, -32.58) * mm});
            skLineSegment(sketch, "E11.40.1", {"start": v(-19.26, -32.58) * mm, "end": v(-19.76, -33.4) * mm});
            skArc(sketch, "E11.40.2", {"start": v(-20.6, -34.05) * mm, "mid": v(-20.14, -33.78) * mm, "end": v(-19.76, -33.4) * mm});
            skArc(sketch, "E11.40.3", {"start": v(-21.04, -33.79) * mm, "mid": v(-20.82, -33.92) * mm, "end": v(-20.6, -34.05) * mm});
            skArc(sketch, "E11.40.4", {"start": v(-21.04, -33.79) * mm, "mid": v(-21, -33.25) * mm, "end": v(-20.83, -32.73) * mm});
            skLineSegment(sketch, "E11.40.5", {"start": v(-20.34, -31.92) * mm, "end": v(-20.83, -32.73) * mm});
            skArc(sketch, "E11.40.6", {"start": v(-20.26, -31.61) * mm, "mid": v(-20.29, -31.77) * mm, "end": v(-20.34, -31.92) * mm});
            skArc(sketch, "E11.41.0", {"start": v(-16.89, -33.54) * mm, "mid": v(-17, -33.64) * mm, "end": v(-17.12, -33.76) * mm});
            skLineSegment(sketch, "E11.41.1", {"start": v(-17.12, -33.76) * mm, "end": v(-17.56, -34.6) * mm});
            skArc(sketch, "E11.41.2", {"start": v(-18.36, -35.31) * mm, "mid": v(-17.91, -35.01) * mm, "end": v(-17.56, -34.6) * mm});
            skArc(sketch, "E11.41.3", {"start": v(-18.8, -35.08) * mm, "mid": v(-18.58, -35.2) * mm, "end": v(-18.36, -35.31) * mm});
            skArc(sketch, "E11.41.4", {"start": v(-18.8, -35.08) * mm, "mid": v(-18.8, -34.54) * mm, "end": v(-18.67, -34.01) * mm});
            skLineSegment(sketch, "E11.41.5", {"start": v(-18.23, -33.17) * mm, "end": v(-18.67, -34.01) * mm});
            skArc(sketch, "E11.41.6", {"start": v(-18.17, -32.86) * mm, "mid": v(-18.19, -33.02) * mm, "end": v(-18.23, -33.17) * mm});
            skArc(sketch, "E11.42.0", {"start": v(-14.68, -34.56) * mm, "mid": v(-14.8, -34.67) * mm, "end": v(-14.9, -34.8) * mm});
            skLineSegment(sketch, "E11.42.1", {"start": v(-14.9, -34.8) * mm, "end": v(-15.28, -35.66) * mm});
            skArc(sketch, "E11.42.2", {"start": v(-16.04, -36.43) * mm, "mid": v(-15.6, -36.1) * mm, "end": v(-15.28, -35.66) * mm});
            skArc(sketch, "E11.42.3", {"start": v(-16.5, -36.22) * mm, "mid": v(-16.27, -36.32) * mm, "end": v(-16.04, -36.43) * mm});
            skArc(sketch, "E11.42.4", {"start": v(-16.5, -36.22) * mm, "mid": v(-16.54, -35.68) * mm, "end": v(-16.43, -35.15) * mm});
            skLineSegment(sketch, "E11.42.5", {"start": v(-16.04, -34.28) * mm, "end": v(-16.43, -35.15) * mm});
            skArc(sketch, "E11.42.6", {"start": v(-16, -33.97) * mm, "mid": v(-16.01, -34.13) * mm, "end": v(-16.04, -34.28) * mm});
            skArc(sketch, "E11.43.0", {"start": v(-12.41, -35.44) * mm, "mid": v(-12.52, -35.56) * mm, "end": v(-12.61, -35.69) * mm});
            skLineSegment(sketch, "E11.43.1", {"start": v(-12.61, -35.69) * mm, "end": v(-12.94, -36.58) * mm});
            skArc(sketch, "E11.43.2", {"start": v(-13.65, -37.39) * mm, "mid": v(-13.24, -37.03) * mm, "end": v(-12.94, -36.58) * mm});
            skArc(sketch, "E11.43.3", {"start": v(-14.12, -37.21) * mm, "mid": v(-13.88, -37.3) * mm, "end": v(-13.65, -37.39) * mm});
            skArc(sketch, "E11.43.4", {"start": v(-14.12, -37.21) * mm, "mid": v(-14.2, -36.68) * mm, "end": v(-14.12, -36.14) * mm});
            skLineSegment(sketch, "E11.43.5", {"start": v(-13.79, -35.25) * mm, "end": v(-14.12, -36.14) * mm});
            skArc(sketch, "E11.43.6", {"start": v(-13.78, -34.93) * mm, "mid": v(-13.77, -35.1) * mm, "end": v(-13.79, -35.25) * mm});
            skArc(sketch, "E11.44.0", {"start": v(-10.1, -36.17) * mm, "mid": v(-10.2, -36.3) * mm, "end": v(-10.27, -36.43) * mm});
            skLineSegment(sketch, "E11.44.1", {"start": v(-10.27, -36.43) * mm, "end": v(-10.55, -37.34) * mm});
            skArc(sketch, "E11.44.2", {"start": v(-11.2, -38.2) * mm, "mid": v(-10.81, -37.81) * mm, "end": v(-10.55, -37.34) * mm});
            skArc(sketch, "E11.44.3", {"start": v(-11.68, -38.05) * mm, "mid": v(-11.44, -38.12) * mm, "end": v(-11.2, -38.2) * mm});
            skArc(sketch, "E11.44.4", {"start": v(-11.68, -38.05) * mm, "mid": v(-11.79, -37.52) * mm, "end": v(-11.75, -36.98) * mm});
            skLineSegment(sketch, "E11.44.5", {"start": v(-11.48, -36.07) * mm, "end": v(-11.75, -36.98) * mm});
            skArc(sketch, "E11.44.6", {"start": v(-11.49, -35.75) * mm, "mid": v(-11.47, -35.9) * mm, "end": v(-11.48, -36.07) * mm});
            skArc(sketch, "E11.45.0", {"start": v(-7.73, -36.75) * mm, "mid": v(-7.82, -36.88) * mm, "end": v(-7.9, -37.02) * mm});
            skLineSegment(sketch, "E11.45.1", {"start": v(-7.9, -37.02) * mm, "end": v(-8.1, -37.94) * mm});
            skArc(sketch, "E11.45.2", {"start": v(-8.7, -38.84) * mm, "mid": v(-8.34, -38.43) * mm, "end": v(-8.1, -37.94) * mm});
            skArc(sketch, "E11.45.3", {"start": v(-9.19, -38.72) * mm, "mid": v(-8.95, -38.78) * mm, "end": v(-8.7, -38.84) * mm});
            skArc(sketch, "E11.45.4", {"start": v(-9.19, -38.72) * mm, "mid": v(-9.33, -38.2) * mm, "end": v(-9.33, -37.66) * mm});
            skLineSegment(sketch, "E11.45.5", {"start": v(-9.12, -36.74) * mm, "end": v(-9.33, -37.66) * mm});
            skArc(sketch, "E11.45.6", {"start": v(-9.15, -36.42) * mm, "mid": v(-9.12, -36.58) * mm, "end": v(-9.12, -36.74) * mm});
            skArc(sketch, "E11.46.0", {"start": v(-5.33, -37.17) * mm, "mid": v(-5.42, -37.3) * mm, "end": v(-5.48, -37.45) * mm});
            skLineSegment(sketch, "E11.46.1", {"start": v(-5.48, -37.45) * mm, "end": v(-5.63, -38.39) * mm});
            skArc(sketch, "E11.46.2", {"start": v(-6.17, -39.32) * mm, "mid": v(-5.84, -38.9) * mm, "end": v(-5.63, -38.39) * mm});
            skArc(sketch, "E11.46.3", {"start": v(-6.66, -39.24) * mm, "mid": v(-6.42, -39.28) * mm, "end": v(-6.17, -39.32) * mm});
            skArc(sketch, "E11.46.4", {"start": v(-6.66, -39.24) * mm, "mid": v(-6.84, -38.73) * mm, "end": v(-6.88, -38.19) * mm});
            skLineSegment(sketch, "E11.46.5", {"start": v(-6.72, -37.25) * mm, "end": v(-6.88, -38.19) * mm});
            skArc(sketch, "E11.46.6", {"start": v(-6.77, -36.93) * mm, "mid": v(-6.73, -37.09) * mm, "end": v(-6.72, -37.25) * mm});
            skArc(sketch, "E11.47.0", {"start": v(-2.92, -37.44) * mm, "mid": v(-3, -37.58) * mm, "end": v(-3.05, -37.73) * mm});
            skLineSegment(sketch, "E11.47.1", {"start": v(-3.05, -37.73) * mm, "end": v(-3.14, -38.67) * mm});
            skArc(sketch, "E11.47.2", {"start": v(-3.61, -39.64) * mm, "mid": v(-3.3, -39.19) * mm, "end": v(-3.14, -38.67) * mm});
            skArc(sketch, "E11.47.3", {"start": v(-4.1, -39.59) * mm, "mid": v(-3.86, -39.61) * mm, "end": v(-3.61, -39.64) * mm});
            skArc(sketch, "E11.47.4", {"start": v(-4.1, -39.59) * mm, "mid": v(-4.32, -39.09) * mm, "end": v(-4.39, -38.55) * mm});
            skLineSegment(sketch, "E11.47.5", {"start": v(-4.3, -37.6) * mm, "end": v(-4.39, -38.55) * mm});
            skArc(sketch, "E11.47.6", {"start": v(-4.37, -37.3) * mm, "mid": v(-4.32, -37.45) * mm, "end": v(-4.3, -37.6) * mm});
            skArc(sketch, "E11.48.0", {"start": v(-0.49, -37.55) * mm, "mid": v(-0.55, -37.7) * mm, "end": v(-0.6, -37.85) * mm});
            skLineSegment(sketch, "E11.48.1", {"start": v(-0.6, -37.85) * mm, "end": v(-0.63, -38.8) * mm});
            skArc(sketch, "E11.48.2", {"start": v(-1.04, -39.79) * mm, "mid": v(-0.77, -39.32) * mm, "end": v(-0.63, -38.8) * mm});
            skArc(sketch, "E11.48.3", {"start": v(-1.54, -39.77) * mm, "mid": v(-1.29, -39.78) * mm, "end": v(-1.04, -39.79) * mm});
            skArc(sketch, "E11.48.4", {"start": v(-1.54, -39.77) * mm, "mid": v(-1.78, -39.29) * mm, "end": v(-1.88, -38.75) * mm});
            skLineSegment(sketch, "E11.48.5", {"start": v(-1.85, -37.8) * mm, "end": v(-1.88, -38.75) * mm});
            skArc(sketch, "E11.48.6", {"start": v(-1.94, -37.5) * mm, "mid": v(-1.89, -37.65) * mm, "end": v(-1.85, -37.8) * mm});
            skArc(sketch, "E11.49.0", {"start": v(1.94, -37.5) * mm, "mid": v(1.89, -37.65) * mm, "end": v(1.85, -37.8) * mm});
            skLineSegment(sketch, "E11.49.1", {"start": v(1.85, -37.8) * mm, "end": v(1.88, -38.75) * mm});
            skArc(sketch, "E11.49.2", {"start": v(1.54, -39.77) * mm, "mid": v(1.78, -39.29) * mm, "end": v(1.88, -38.75) * mm});
            skArc(sketch, "E11.49.3", {"start": v(1.04, -39.79) * mm, "mid": v(1.29, -39.78) * mm, "end": v(1.54, -39.77) * mm});
            skArc(sketch, "E11.49.4", {"start": v(1.04, -39.79) * mm, "mid": v(0.77, -39.32) * mm, "end": v(0.63, -38.8) * mm});
            skLineSegment(sketch, "E11.49.5", {"start": v(0.6, -37.85) * mm, "end": v(0.63, -38.8) * mm});
            skArc(sketch, "E11.49.6", {"start": v(0.49, -37.55) * mm, "mid": v(0.55, -37.7) * mm, "end": v(0.6, -37.85) * mm});
            skArc(sketch, "E11.50.0", {"start": v(4.37, -37.3) * mm, "mid": v(4.32, -37.45) * mm, "end": v(4.3, -37.6) * mm});
            skLineSegment(sketch, "E11.50.1", {"start": v(4.3, -37.6) * mm, "end": v(4.39, -38.55) * mm});
            skArc(sketch, "E11.50.2", {"start": v(4.1, -39.59) * mm, "mid": v(4.32, -39.09) * mm, "end": v(4.39, -38.55) * mm});
            skArc(sketch, "E11.50.3", {"start": v(3.61, -39.64) * mm, "mid": v(3.86, -39.61) * mm, "end": v(4.1, -39.59) * mm});
            skArc(sketch, "E11.50.4", {"start": v(3.61, -39.64) * mm, "mid": v(3.3, -39.19) * mm, "end": v(3.14, -38.67) * mm});
            skLineSegment(sketch, "E11.50.5", {"start": v(3.05, -37.73) * mm, "end": v(3.14, -38.67) * mm});
            skArc(sketch, "E11.50.6", {"start": v(2.92, -37.44) * mm, "mid": v(3, -37.58) * mm, "end": v(3.05, -37.73) * mm});
            skArc(sketch, "E11.51.0", {"start": v(6.77, -36.93) * mm, "mid": v(6.73, -37.09) * mm, "end": v(6.72, -37.25) * mm});
            skLineSegment(sketch, "E11.51.1", {"start": v(6.72, -37.25) * mm, "end": v(6.88, -38.19) * mm});
            skArc(sketch, "E11.51.2", {"start": v(6.66, -39.24) * mm, "mid": v(6.84, -38.73) * mm, "end": v(6.88, -38.19) * mm});
            skArc(sketch, "E11.51.3", {"start": v(6.17, -39.32) * mm, "mid": v(6.42, -39.28) * mm, "end": v(6.66, -39.24) * mm});
            skArc(sketch, "E11.51.4", {"start": v(6.17, -39.32) * mm, "mid": v(5.84, -38.9) * mm, "end": v(5.63, -38.39) * mm});
            skLineSegment(sketch, "E11.51.5", {"start": v(5.48, -37.45) * mm, "end": v(5.63, -38.39) * mm});
            skArc(sketch, "E11.51.6", {"start": v(5.33, -37.17) * mm, "mid": v(5.42, -37.3) * mm, "end": v(5.48, -37.45) * mm});
            skArc(sketch, "E11.52.0", {"start": v(9.15, -36.42) * mm, "mid": v(9.12, -36.58) * mm, "end": v(9.12, -36.74) * mm});
            skLineSegment(sketch, "E11.52.1", {"start": v(9.12, -36.74) * mm, "end": v(9.33, -37.66) * mm});
            skArc(sketch, "E11.52.2", {"start": v(9.19, -38.72) * mm, "mid": v(9.33, -38.2) * mm, "end": v(9.33, -37.66) * mm});
            skArc(sketch, "E11.52.3", {"start": v(8.7, -38.84) * mm, "mid": v(8.95, -38.78) * mm, "end": v(9.19, -38.72) * mm});
            skArc(sketch, "E11.52.4", {"start": v(8.7, -38.84) * mm, "mid": v(8.34, -38.43) * mm, "end": v(8.1, -37.94) * mm});
            skLineSegment(sketch, "E11.52.5", {"start": v(7.9, -37.02) * mm, "end": v(8.1, -37.94) * mm});
            skArc(sketch, "E11.52.6", {"start": v(7.73, -36.75) * mm, "mid": v(7.82, -36.88) * mm, "end": v(7.9, -37.02) * mm});
            skArc(sketch, "E11.53.0", {"start": v(11.49, -35.75) * mm, "mid": v(11.47, -35.9) * mm, "end": v(11.48, -36.07) * mm});
            skLineSegment(sketch, "E11.53.1", {"start": v(11.48, -36.07) * mm, "end": v(11.75, -36.98) * mm});
            skArc(sketch, "E11.53.2", {"start": v(11.68, -38.05) * mm, "mid": v(11.79, -37.52) * mm, "end": v(11.75, -36.98) * mm});
            skArc(sketch, "E11.53.3", {"start": v(11.2, -38.2) * mm, "mid": v(11.44, -38.12) * mm, "end": v(11.68, -38.05) * mm});
            skArc(sketch, "E11.53.4", {"start": v(11.2, -38.2) * mm, "mid": v(10.81, -37.81) * mm, "end": v(10.55, -37.34) * mm});
            skLineSegment(sketch, "E11.53.5", {"start": v(10.27, -36.43) * mm, "end": v(10.55, -37.34) * mm});
            skArc(sketch, "E11.53.6", {"start": v(10.1, -36.17) * mm, "mid": v(10.2, -36.3) * mm, "end": v(10.27, -36.43) * mm});
            skArc(sketch, "E11.54.0", {"start": v(13.78, -34.93) * mm, "mid": v(13.77, -35.1) * mm, "end": v(13.79, -35.25) * mm});
            skLineSegment(sketch, "E11.54.1", {"start": v(13.79, -35.25) * mm, "end": v(14.12, -36.14) * mm});
            skArc(sketch, "E11.54.2", {"start": v(14.12, -37.21) * mm, "mid": v(14.2, -36.68) * mm, "end": v(14.12, -36.14) * mm});
            skArc(sketch, "E11.54.3", {"start": v(13.65, -37.39) * mm, "mid": v(13.88, -37.3) * mm, "end": v(14.12, -37.21) * mm});
            skArc(sketch, "E11.54.4", {"start": v(13.65, -37.39) * mm, "mid": v(13.24, -37.03) * mm, "end": v(12.94, -36.58) * mm});
            skLineSegment(sketch, "E11.54.5", {"start": v(12.61, -35.69) * mm, "end": v(12.94, -36.58) * mm});
            skArc(sketch, "E11.54.6", {"start": v(12.41, -35.44) * mm, "mid": v(12.52, -35.56) * mm, "end": v(12.61, -35.69) * mm});
            skArc(sketch, "E11.55.0", {"start": v(16, -33.97) * mm, "mid": v(16.01, -34.13) * mm, "end": v(16.04, -34.28) * mm});
            skLineSegment(sketch, "E11.55.1", {"start": v(16.04, -34.28) * mm, "end": v(16.43, -35.15) * mm});
            skArc(sketch, "E11.55.2", {"start": v(16.5, -36.22) * mm, "mid": v(16.54, -35.68) * mm, "end": v(16.43, -35.15) * mm});
            skArc(sketch, "E11.55.3", {"start": v(16.04, -36.43) * mm, "mid": v(16.27, -36.32) * mm, "end": v(16.5, -36.22) * mm});
            skArc(sketch, "E11.55.4", {"start": v(16.04, -36.43) * mm, "mid": v(15.6, -36.1) * mm, "end": v(15.28, -35.66) * mm});
            skLineSegment(sketch, "E11.55.5", {"start": v(14.9, -34.8) * mm, "end": v(15.28, -35.66) * mm});
            skArc(sketch, "E11.55.6", {"start": v(14.68, -34.56) * mm, "mid": v(14.8, -34.67) * mm, "end": v(14.9, -34.8) * mm});
            skArc(sketch, "E11.56.0", {"start": v(18.17, -32.86) * mm, "mid": v(18.19, -33.02) * mm, "end": v(18.23, -33.17) * mm});
            skLineSegment(sketch, "E11.56.1", {"start": v(18.23, -33.17) * mm, "end": v(18.67, -34.01) * mm});
            skArc(sketch, "E11.56.2", {"start": v(18.8, -35.08) * mm, "mid": v(18.8, -34.54) * mm, "end": v(18.67, -34.01) * mm});
            skArc(sketch, "E11.56.3", {"start": v(18.36, -35.31) * mm, "mid": v(18.58, -35.2) * mm, "end": v(18.8, -35.08) * mm});
            skArc(sketch, "E11.56.4", {"start": v(18.36, -35.31) * mm, "mid": v(17.91, -35.01) * mm, "end": v(17.56, -34.6) * mm});
            skLineSegment(sketch, "E11.56.5", {"start": v(17.12, -33.76) * mm, "end": v(17.56, -34.6) * mm});
            skArc(sketch, "E11.56.6", {"start": v(16.89, -33.54) * mm, "mid": v(17, -33.64) * mm, "end": v(17.12, -33.76) * mm});
            skArc(sketch, "E11.57.0", {"start": v(20.26, -31.61) * mm, "mid": v(20.29, -31.77) * mm, "end": v(20.34, -31.92) * mm});
            skLineSegment(sketch, "E11.57.1", {"start": v(20.34, -31.92) * mm, "end": v(20.83, -32.73) * mm});
            skArc(sketch, "E11.57.2", {"start": v(21.04, -33.79) * mm, "mid": v(21, -33.25) * mm, "end": v(20.83, -32.73) * mm});
            skArc(sketch, "E11.57.3", {"start": v(20.6, -34.05) * mm, "mid": v(20.82, -33.92) * mm, "end": v(21.04, -33.79) * mm});
            skArc(sketch, "E11.57.4", {"start": v(20.6, -34.05) * mm, "mid": v(20.14, -33.78) * mm, "end": v(19.76, -33.4) * mm});
            skLineSegment(sketch, "E11.57.5", {"start": v(19.26, -32.58) * mm, "end": v(19.76, -33.4) * mm});
            skArc(sketch, "E11.57.6", {"start": v(19.02, -32.38) * mm, "mid": v(19.15, -32.47) * mm, "end": v(19.26, -32.58) * mm});
            skArc(sketch, "E11.58.0", {"start": v(22.27, -30.24) * mm, "mid": v(22.3, -30.4) * mm, "end": v(22.36, -30.54) * mm});
            skLineSegment(sketch, "E11.58.1", {"start": v(22.36, -30.54) * mm, "end": v(22.9, -31.32) * mm});
            skArc(sketch, "E11.58.2", {"start": v(23.18, -32.35) * mm, "mid": v(23.11, -31.82) * mm, "end": v(22.9, -31.32) * mm});
            skArc(sketch, "E11.58.3", {"start": v(22.77, -32.64) * mm, "mid": v(22.97, -32.5) * mm, "end": v(23.18, -32.35) * mm});
            skArc(sketch, "E11.58.4", {"start": v(22.77, -32.64) * mm, "mid": v(22.28, -32.4) * mm, "end": v(21.88, -32.04) * mm});
            skLineSegment(sketch, "E11.58.5", {"start": v(21.33, -31.27) * mm, "end": v(21.88, -32.04) * mm});
            skArc(sketch, "E11.58.6", {"start": v(21.08, -31.08) * mm, "mid": v(21.21, -31.16) * mm, "end": v(21.33, -31.27) * mm});
            skArc(sketch, "E11.59.0", {"start": v(24.18, -28.73) * mm, "mid": v(24.22, -28.88) * mm, "end": v(24.29, -29.03) * mm});
            skLineSegment(sketch, "E11.59.1", {"start": v(24.29, -29.03) * mm, "end": v(24.89, -29.77) * mm});
            skArc(sketch, "E11.59.2", {"start": v(25.22, -30.79) * mm, "mid": v(25.13, -30.25) * mm, "end": v(24.89, -29.77) * mm});
            skArc(sketch, "E11.59.3", {"start": v(24.84, -31.1) * mm, "mid": v(25.03, -30.94) * mm, "end": v(25.22, -30.79) * mm});
            skArc(sketch, "E11.59.4", {"start": v(24.84, -31.1) * mm, "mid": v(24.34, -30.9) * mm, "end": v(23.9, -30.56) * mm});
            skLineSegment(sketch, "E11.59.5", {"start": v(23.31, -29.82) * mm, "end": v(23.9, -30.56) * mm});
            skArc(sketch, "E11.59.6", {"start": v(23.04, -29.65) * mm, "mid": v(23.19, -29.72) * mm, "end": v(23.31, -29.82) * mm});
            skArc(sketch, "E11.60.0", {"start": v(25.99, -27.1) * mm, "mid": v(26.04, -27.26) * mm, "end": v(26.12, -27.4) * mm});
            skLineSegment(sketch, "E11.60.1", {"start": v(26.12, -27.4) * mm, "end": v(26.76, -28.1) * mm});
            skArc(sketch, "E11.60.2", {"start": v(27.16, -29.09) * mm, "mid": v(27.03, -28.56) * mm, "end": v(26.76, -28.1) * mm});
            skArc(sketch, "E11.60.3", {"start": v(26.8, -29.43) * mm, "mid": v(26.98, -29.26) * mm, "end": v(27.16, -29.09) * mm});
            skArc(sketch, "E11.60.4", {"start": v(26.8, -29.43) * mm, "mid": v(26.28, -29.25) * mm, "end": v(25.84, -28.95) * mm});
            skLineSegment(sketch, "E11.60.5", {"start": v(25.2, -28.25) * mm, "end": v(25.84, -28.95) * mm});
            skArc(sketch, "E11.60.6", {"start": v(24.92, -28.1) * mm, "mid": v(25.06, -28.16) * mm, "end": v(25.2, -28.25) * mm});
            skArc(sketch, "E11.61.0", {"start": v(27.69, -25.37) * mm, "mid": v(27.75, -25.51) * mm, "end": v(27.84, -25.65) * mm});
            skLineSegment(sketch, "E11.61.1", {"start": v(27.84, -25.65) * mm, "end": v(28.52, -26.3) * mm});
            skArc(sketch, "E11.61.2", {"start": v(28.99, -27.27) * mm, "mid": v(28.82, -26.75) * mm, "end": v(28.52, -26.3) * mm});
            skArc(sketch, "E11.61.3", {"start": v(28.65, -27.63) * mm, "mid": v(28.82, -27.45) * mm, "end": v(28.99, -27.27) * mm});
            skArc(sketch, "E11.61.4", {"start": v(28.65, -27.63) * mm, "mid": v(28.12, -27.49) * mm, "end": v(27.66, -27.21) * mm});
            skLineSegment(sketch, "E11.61.5", {"start": v(26.97, -26.56) * mm, "end": v(27.66, -27.21) * mm});
            skArc(sketch, "E11.61.6", {"start": v(26.68, -26.42) * mm, "mid": v(26.83, -26.48) * mm, "end": v(26.97, -26.56) * mm});
            skArc(sketch, "E11.62.0", {"start": v(29.27, -23.52) * mm, "mid": v(29.34, -23.66) * mm, "end": v(29.44, -23.8) * mm});
            skLineSegment(sketch, "E11.62.1", {"start": v(29.44, -23.8) * mm, "end": v(30.17, -24.4) * mm});
            skArc(sketch, "E11.62.2", {"start": v(30.7, -25.34) * mm, "mid": v(30.5, -24.83) * mm, "end": v(30.17, -24.4) * mm});
            skArc(sketch, "E11.62.3", {"start": v(30.37, -25.72) * mm, "mid": v(30.53, -25.53) * mm, "end": v(30.7, -25.34) * mm});
            skArc(sketch, "E11.62.4", {"start": v(30.37, -25.72) * mm, "mid": v(29.84, -25.61) * mm, "end": v(29.36, -25.37) * mm});
            skLineSegment(sketch, "E11.62.5", {"start": v(28.63, -24.76) * mm, "end": v(29.36, -25.37) * mm});
            skArc(sketch, "E11.62.6", {"start": v(28.34, -24.64) * mm, "mid": v(28.49, -24.69) * mm, "end": v(28.63, -24.76) * mm});
            skArc(sketch, "E11.63.0", {"start": v(30.73, -21.58) * mm, "mid": v(30.81, -21.71) * mm, "end": v(30.92, -21.84) * mm});
            skLineSegment(sketch, "E11.63.1", {"start": v(30.92, -21.84) * mm, "end": v(31.68, -22.4) * mm});
            skArc(sketch, "E11.63.2", {"start": v(32.27, -23.3) * mm, "mid": v(32.04, -22.8) * mm, "end": v(31.68, -22.4) * mm});
            skArc(sketch, "E11.63.3", {"start": v(31.97, -23.7) * mm, "mid": v(32.12, -23.5) * mm, "end": v(32.27, -23.3) * mm});
            skArc(sketch, "E11.63.4", {"start": v(31.97, -23.7) * mm, "mid": v(31.44, -23.63) * mm, "end": v(30.94, -23.41) * mm});
            skLineSegment(sketch, "E11.63.5", {"start": v(30.17, -22.85) * mm, "end": v(30.94, -23.41) * mm});
            skArc(sketch, "E11.63.6", {"start": v(29.87, -22.75) * mm, "mid": v(30.03, -22.79) * mm, "end": v(30.17, -22.85) * mm});
            skArc(sketch, "E11.64.0", {"start": v(32.06, -19.54) * mm, "mid": v(32.15, -19.67) * mm, "end": v(32.26, -19.79) * mm});
            skLineSegment(sketch, "E11.64.1", {"start": v(32.26, -19.79) * mm, "end": v(33.07, -20.3) * mm});
            skArc(sketch, "E11.64.2", {"start": v(33.71, -21.16) * mm, "mid": v(33.45, -20.68) * mm, "end": v(33.07, -20.3) * mm});
            skArc(sketch, "E11.64.3", {"start": v(33.44, -21.58) * mm, "mid": v(33.58, -21.37) * mm, "end": v(33.71, -21.16) * mm});
            skArc(sketch, "E11.64.4", {"start": v(33.44, -21.58) * mm, "mid": v(32.9, -21.54) * mm, "end": v(32.4, -21.36) * mm});
            skLineSegment(sketch, "E11.64.5", {"start": v(31.59, -20.85) * mm, "end": v(32.4, -21.36) * mm});
            skArc(sketch, "E11.64.6", {"start": v(31.28, -20.77) * mm, "mid": v(31.44, -20.8) * mm, "end": v(31.59, -20.85) * mm});
            skArc(sketch, "E11.65.0", {"start": v(33.26, -17.43) * mm, "mid": v(33.36, -17.55) * mm, "end": v(33.48, -17.66) * mm});
            skLineSegment(sketch, "E11.65.1", {"start": v(33.48, -17.66) * mm, "end": v(34.31, -18.12) * mm});
            skArc(sketch, "E11.65.2", {"start": v(35, -18.93) * mm, "mid": v(34.72, -18.48) * mm, "end": v(34.31, -18.12) * mm});
            skArc(sketch, "E11.65.3", {"start": v(34.77, -19.37) * mm, "mid": v(34.89, -19.15) * mm, "end": v(35, -18.93) * mm});
            skArc(sketch, "E11.65.4", {"start": v(34.77, -19.37) * mm, "mid": v(34.23, -19.37) * mm, "end": v(33.7, -19.22) * mm});
            skLineSegment(sketch, "E11.65.5", {"start": v(32.87, -18.76) * mm, "end": v(33.7, -19.22) * mm});
            skArc(sketch, "E11.65.6", {"start": v(32.56, -18.7) * mm, "mid": v(32.72, -18.72) * mm, "end": v(32.87, -18.76) * mm});
            skArc(sketch, "E11.66.0", {"start": v(34.32, -15.24) * mm, "mid": v(34.43, -15.36) * mm, "end": v(34.55, -15.46) * mm});
            skLineSegment(sketch, "E11.66.1", {"start": v(34.55, -15.46) * mm, "end": v(35.41, -15.86) * mm});
            skArc(sketch, "E11.66.2", {"start": v(36.16, -16.63) * mm, "mid": v(35.84, -16.2) * mm, "end": v(35.41, -15.86) * mm});
            skArc(sketch, "E11.66.3", {"start": v(35.95, -17.08) * mm, "mid": v(36.06, -16.85) * mm, "end": v(36.16, -16.63) * mm});
            skArc(sketch, "E11.66.4", {"start": v(35.95, -17.08) * mm, "mid": v(35.4, -17.11) * mm, "end": v(34.88, -17) * mm});
            skLineSegment(sketch, "E11.66.5", {"start": v(34.02, -16.6) * mm, "end": v(34.88, -17) * mm});
            skArc(sketch, "E11.66.6", {"start": v(33.7, -16.56) * mm, "mid": v(33.86, -16.56) * mm, "end": v(34.02, -16.6) * mm});
            skArc(sketch, "E11.67.0", {"start": v(35.23, -12.98) * mm, "mid": v(35.35, -13.1) * mm, "end": v(35.48, -13.19) * mm});
            skLineSegment(sketch, "E11.67.1", {"start": v(35.48, -13.19) * mm, "end": v(36.36, -13.53) * mm});
            skArc(sketch, "E11.67.2", {"start": v(37.16, -14.25) * mm, "mid": v(36.81, -13.84) * mm, "end": v(36.36, -13.53) * mm});
            skArc(sketch, "E11.67.3", {"start": v(36.98, -14.72) * mm, "mid": v(37.07, -14.48) * mm, "end": v(37.16, -14.25) * mm});
            skArc(sketch, "E11.67.4", {"start": v(36.98, -14.72) * mm, "mid": v(36.44, -14.78) * mm, "end": v(35.9, -14.7) * mm});
            skLineSegment(sketch, "E11.67.5", {"start": v(35.02, -14.36) * mm, "end": v(35.9, -14.7) * mm});
            skArc(sketch, "E11.67.6", {"start": v(34.7, -14.34) * mm, "mid": v(34.86, -14.34) * mm, "end": v(35.02, -14.36) * mm});
            skArc(sketch, "E11.68.0", {"start": v(36, -10.68) * mm, "mid": v(36.12, -10.78) * mm, "end": v(36.26, -10.86) * mm});
            skLineSegment(sketch, "E11.68.1", {"start": v(36.26, -10.86) * mm, "end": v(37.16, -11.15) * mm});
            skArc(sketch, "E11.68.2", {"start": v(38, -11.81) * mm, "mid": v(37.63, -11.43) * mm, "end": v(37.16, -11.15) * mm});
            skArc(sketch, "E11.68.3", {"start": v(37.85, -12.3) * mm, "mid": v(37.93, -12.05) * mm, "end": v(38, -11.81) * mm});
            skArc(sketch, "E11.68.4", {"start": v(37.85, -12.3) * mm, "mid": v(37.32, -12.4) * mm, "end": v(36.78, -12.35) * mm});
            skLineSegment(sketch, "E11.68.5", {"start": v(35.88, -12.06) * mm, "end": v(36.78, -12.35) * mm});
            skArc(sketch, "E11.68.6", {"start": v(35.56, -12.06) * mm, "mid": v(35.72, -12.05) * mm, "end": v(35.88, -12.06) * mm});
            skArc(sketch, "E11.69.0", {"start": v(36.62, -8.32) * mm, "mid": v(36.74, -8.42) * mm, "end": v(36.88, -8.5) * mm});
            skLineSegment(sketch, "E11.69.1", {"start": v(36.88, -8.5) * mm, "end": v(37.8, -8.72) * mm});
            skArc(sketch, "E11.69.2", {"start": v(38.7, -9.33) * mm, "mid": v(38.3, -8.97) * mm, "end": v(37.8, -8.72) * mm});
            skArc(sketch, "E11.69.3", {"start": v(38.57, -9.82) * mm, "mid": v(38.63, -9.57) * mm, "end": v(38.7, -9.33) * mm});
            skArc(sketch, "E11.69.4", {"start": v(38.57, -9.82) * mm, "mid": v(38.05, -9.95) * mm, "end": v(37.5, -9.94) * mm});
            skLineSegment(sketch, "E11.69.5", {"start": v(36.58, -9.71) * mm, "end": v(37.5, -9.94) * mm});
            skArc(sketch, "E11.69.6", {"start": v(36.27, -9.74) * mm, "mid": v(36.42, -9.71) * mm, "end": v(36.58, -9.71) * mm});
            skArc(sketch, "E11.70.0", {"start": v(37.08, -5.94) * mm, "mid": v(37.21, -6.02) * mm, "end": v(37.36, -6.09) * mm});
            skLineSegment(sketch, "E11.70.1", {"start": v(37.36, -6.09) * mm, "end": v(38.3, -6.26) * mm});
            skArc(sketch, "E11.70.2", {"start": v(39.21, -6.8) * mm, "mid": v(38.8, -6.47) * mm, "end": v(38.3, -6.26) * mm});
            skArc(sketch, "E11.70.3", {"start": v(39.13, -7.3) * mm, "mid": v(39.17, -7.05) * mm, "end": v(39.21, -6.8) * mm});
            skArc(sketch, "E11.70.4", {"start": v(39.13, -7.3) * mm, "mid": v(38.61, -7.47) * mm, "end": v(38.07, -7.5) * mm});
            skLineSegment(sketch, "E11.70.5", {"start": v(37.13, -7.32) * mm, "end": v(38.07, -7.5) * mm});
            skArc(sketch, "E11.70.6", {"start": v(36.82, -7.37) * mm, "mid": v(36.98, -7.33) * mm, "end": v(37.13, -7.32) * mm});
            skArc(sketch, "E11.71.0", {"start": v(37.38, -3.52) * mm, "mid": v(37.52, -3.6) * mm, "end": v(37.67, -3.66) * mm});
            skLineSegment(sketch, "E11.71.1", {"start": v(37.67, -3.66) * mm, "end": v(38.62, -3.76) * mm});
            skArc(sketch, "E11.71.2", {"start": v(39.57, -4.25) * mm, "mid": v(39.13, -3.94) * mm, "end": v(38.62, -3.76) * mm});
            skArc(sketch, "E11.71.3", {"start": v(39.52, -4.75) * mm, "mid": v(39.54, -4.5) * mm, "end": v(39.57, -4.25) * mm});
            skArc(sketch, "E11.71.4", {"start": v(39.52, -4.75) * mm, "mid": v(39.01, -4.95) * mm, "end": v(38.47, -5.01) * mm});
            skLineSegment(sketch, "E11.71.5", {"start": v(37.53, -4.9) * mm, "end": v(38.47, -5.01) * mm});
            skArc(sketch, "E11.71.6", {"start": v(37.22, -4.97) * mm, "mid": v(37.37, -4.93) * mm, "end": v(37.53, -4.9) * mm});
            skArc(sketch, "E11.72.0", {"start": v(37.53, -1.1) * mm, "mid": v(37.68, -1.16) * mm, "end": v(37.83, -1.21) * mm});
            skLineSegment(sketch, "E11.72.1", {"start": v(37.83, -1.21) * mm, "end": v(38.78, -1.26) * mm});
            skArc(sketch, "E11.72.2", {"start": v(39.76, -1.68) * mm, "mid": v(39.3, -1.4) * mm, "end": v(38.78, -1.26) * mm});
            skArc(sketch, "E11.72.3", {"start": v(39.74, -2.18) * mm, "mid": v(39.75, -1.93) * mm, "end": v(39.76, -1.68) * mm});
            skArc(sketch, "E11.72.4", {"start": v(39.74, -2.18) * mm, "mid": v(39.25, -2.42) * mm, "end": v(38.72, -2.51) * mm});
            skLineSegment(sketch, "E11.72.5", {"start": v(37.77, -2.47) * mm, "end": v(38.72, -2.51) * mm});
            skArc(sketch, "E11.72.6", {"start": v(37.46, -2.55) * mm, "mid": v(37.61, -2.5) * mm, "end": v(37.77, -2.47) * mm});
            skArc(sketch, "E11.73.0", {"start": v(37.53, 1.34) * mm, "mid": v(37.67, 1.28) * mm, "end": v(37.83, 1.24) * mm});
            skLineSegment(sketch, "E11.73.1", {"start": v(37.83, 1.24) * mm, "end": v(38.78, 1.26) * mm});
            skArc(sketch, "E11.73.2", {"start": v(39.79, 0.9) * mm, "mid": v(39.3, 1.14) * mm, "end": v(38.78, 1.26) * mm});
            skArc(sketch, "E11.73.3", {"start": v(39.8, 0.4) * mm, "mid": v(39.8, 0.64) * mm, "end": v(39.79, 0.9) * mm});
            skArc(sketch, "E11.73.4", {"start": v(39.8, 0.4) * mm, "mid": v(39.33, 0.13) * mm, "end": v(38.8, 0) * mm});
            skLineSegment(sketch, "E11.73.5", {"start": v(37.85, -0.02) * mm, "end": v(38.8, 0) * mm});
            skArc(sketch, "E11.73.6", {"start": v(37.55, -0.12) * mm, "mid": v(37.7, -0.06) * mm, "end": v(37.85, -0.02) * mm});
            skArc(sketch, "E11.74.0", {"start": v(37.36, 3.76) * mm, "mid": v(37.51, 3.71) * mm, "end": v(37.67, 3.69) * mm});
            skLineSegment(sketch, "E11.74.1", {"start": v(37.67, 3.69) * mm, "end": v(38.62, 3.76) * mm});
            skArc(sketch, "E11.74.2", {"start": v(39.65, 3.47) * mm, "mid": v(39.15, 3.69) * mm, "end": v(38.62, 3.76) * mm});
            skArc(sketch, "E11.74.3", {"start": v(39.69, 2.97) * mm, "mid": v(39.67, 3.22) * mm, "end": v(39.65, 3.47) * mm});
            skArc(sketch, "E11.74.4", {"start": v(39.69, 2.97) * mm, "mid": v(39.24, 2.67) * mm, "end": v(38.72, 2.51) * mm});
            skLineSegment(sketch, "E11.74.5", {"start": v(37.77, 2.43) * mm, "end": v(38.72, 2.51) * mm});
            skArc(sketch, "E11.74.6", {"start": v(37.48, 2.31) * mm, "mid": v(37.62, 2.38) * mm, "end": v(37.77, 2.43) * mm});
            skArc(sketch, "E11.75.0", {"start": v(37.04, 6.17) * mm, "mid": v(37.2, 6.13) * mm, "end": v(37.35, 6.12) * mm});
            skLineSegment(sketch, "E11.75.1", {"start": v(37.35, 6.12) * mm, "end": v(38.3, 6.26) * mm});
            skArc(sketch, "E11.75.2", {"start": v(39.34, 6.03) * mm, "mid": v(38.83, 6.21) * mm, "end": v(38.3, 6.26) * mm});
            skArc(sketch, "E11.75.3", {"start": v(39.41, 5.53) * mm, "mid": v(39.38, 5.78) * mm, "end": v(39.34, 6.03) * mm});
            skArc(sketch, "E11.75.4", {"start": v(39.41, 5.53) * mm, "mid": v(38.98, 5.2) * mm, "end": v(38.47, 5.01) * mm});
            skLineSegment(sketch, "E11.75.5", {"start": v(37.53, 4.87) * mm, "end": v(38.47, 5.01) * mm});
            skArc(sketch, "E11.75.6", {"start": v(37.25, 4.73) * mm, "mid": v(37.39, 4.81) * mm, "end": v(37.53, 4.87) * mm});
            skArc(sketch, "E11.76.0", {"start": v(36.56, 8.56) * mm, "mid": v(36.72, 8.53) * mm, "end": v(36.88, 8.52) * mm});
            skLineSegment(sketch, "E11.76.1", {"start": v(36.88, 8.52) * mm, "end": v(37.8, 8.72) * mm});
            skArc(sketch, "E11.76.2", {"start": v(38.87, 8.56) * mm, "mid": v(38.35, 8.71) * mm, "end": v(37.8, 8.72) * mm});
            skArc(sketch, "E11.76.3", {"start": v(38.97, 8.07) * mm, "mid": v(38.92, 8.32) * mm, "end": v(38.87, 8.56) * mm});
            skArc(sketch, "E11.76.4", {"start": v(38.97, 8.07) * mm, "mid": v(38.56, 7.72) * mm, "end": v(38.07, 7.5) * mm});
            skLineSegment(sketch, "E11.76.5", {"start": v(37.14, 7.3) * mm, "end": v(38.07, 7.5) * mm});
            skArc(sketch, "E11.76.6", {"start": v(36.87, 7.13) * mm, "mid": v(37, 7.22) * mm, "end": v(37.14, 7.3) * mm});
            skArc(sketch, "E11.77.0", {"start": v(35.93, 10.9) * mm, "mid": v(36.09, 10.89) * mm, "end": v(36.25, 10.9) * mm});
            skLineSegment(sketch, "E11.77.1", {"start": v(36.25, 10.9) * mm, "end": v(37.16, 11.15) * mm});
            skArc(sketch, "E11.77.2", {"start": v(38.23, 11.06) * mm, "mid": v(37.7, 11.18) * mm, "end": v(37.16, 11.15) * mm});
            skArc(sketch, "E11.77.3", {"start": v(38.37, 10.58) * mm, "mid": v(38.3, 10.82) * mm, "end": v(38.23, 11.06) * mm});
            skArc(sketch, "E11.77.4", {"start": v(38.37, 10.58) * mm, "mid": v(37.98, 10.2) * mm, "end": v(37.5, 9.94) * mm});
            skLineSegment(sketch, "E11.77.5", {"start": v(36.6, 9.68) * mm, "end": v(37.5, 9.94) * mm});
            skArc(sketch, "E11.77.6", {"start": v(36.33, 9.5) * mm, "mid": v(36.45, 9.6) * mm, "end": v(36.6, 9.68) * mm});
            skArc(sketch, "E11.78.0", {"start": v(35.15, 13.2) * mm, "mid": v(35.3, 13.2) * mm, "end": v(35.47, 13.22) * mm});
            skLineSegment(sketch, "E11.78.1", {"start": v(35.47, 13.22) * mm, "end": v(36.36, 13.53) * mm});
            skArc(sketch, "E11.78.2", {"start": v(37.44, 13.51) * mm, "mid": v(36.9, 13.6) * mm, "end": v(36.36, 13.53) * mm});
            skArc(sketch, "E11.78.3", {"start": v(37.6, 13.04) * mm, "mid": v(37.52, 13.28) * mm, "end": v(37.44, 13.51) * mm});
            skArc(sketch, "E11.78.4", {"start": v(37.6, 13.04) * mm, "mid": v(37.24, 12.64) * mm, "end": v(36.78, 12.35) * mm});
            skLineSegment(sketch, "E11.78.5", {"start": v(35.89, 12.03) * mm, "end": v(36.78, 12.35) * mm});
            skArc(sketch, "E11.78.6", {"start": v(35.64, 11.84) * mm, "mid": v(35.75, 11.94) * mm, "end": v(35.89, 12.03) * mm});
            skArc(sketch, "E11.79.0", {"start": v(34.22, 15.46) * mm, "mid": v(34.38, 15.46) * mm, "end": v(34.54, 15.48) * mm});
            skLineSegment(sketch, "E11.79.1", {"start": v(34.54, 15.48) * mm, "end": v(35.41, 15.86) * mm});
            skArc(sketch, "E11.79.2", {"start": v(36.48, 15.9) * mm, "mid": v(35.94, 15.96) * mm, "end": v(35.41, 15.86) * mm});
            skArc(sketch, "E11.79.3", {"start": v(36.68, 15.45) * mm, "mid": v(36.58, 15.68) * mm, "end": v(36.48, 15.9) * mm});
            skArc(sketch, "E11.79.4", {"start": v(36.68, 15.45) * mm, "mid": v(36.34, 15.02) * mm, "end": v(35.9, 14.7) * mm});
            skLineSegment(sketch, "E11.79.5", {"start": v(35.03, 14.33) * mm, "end": v(35.9, 14.7) * mm});
            skArc(sketch, "E11.79.6", {"start": v(34.8, 14.12) * mm, "mid": v(34.9, 14.23) * mm, "end": v(35.03, 14.33) * mm});
            skArc(sketch, "E11.80.0", {"start": v(33.15, 17.64) * mm, "mid": v(33.3, 17.65) * mm, "end": v(33.46, 17.69) * mm});
            skLineSegment(sketch, "E11.80.1", {"start": v(33.46, 17.69) * mm, "end": v(34.31, 18.12) * mm});
            skArc(sketch, "E11.80.2", {"start": v(35.38, 18.23) * mm, "mid": v(34.84, 18.25) * mm, "end": v(34.31, 18.12) * mm});
            skArc(sketch, "E11.80.3", {"start": v(35.6, 17.79) * mm, "mid": v(35.5, 18.01) * mm, "end": v(35.38, 18.23) * mm});
            skArc(sketch, "E11.80.4", {"start": v(35.6, 17.79) * mm, "mid": v(35.3, 17.34) * mm, "end": v(34.88, 17) * mm});
            skLineSegment(sketch, "E11.80.5", {"start": v(34.03, 16.57) * mm, "end": v(34.88, 17) * mm});
            skArc(sketch, "E11.80.6", {"start": v(33.8, 16.34) * mm, "mid": v(33.91, 16.46) * mm, "end": v(34.03, 16.57) * mm});
            skArc(sketch, "E11.81.0", {"start": v(31.94, 19.75) * mm, "mid": v(32.1, 19.77) * mm, "end": v(32.25, 19.82) * mm});
            skLineSegment(sketch, "E11.81.1", {"start": v(32.25, 19.82) * mm, "end": v(33.07, 20.3) * mm});
            skArc(sketch, "E11.81.2", {"start": v(34.12, 20.49) * mm, "mid": v(33.58, 20.46) * mm, "end": v(33.07, 20.3) * mm});
            skArc(sketch, "E11.81.3", {"start": v(34.38, 20.06) * mm, "mid": v(34.25, 20.27) * mm, "end": v(34.12, 20.49) * mm});
            skArc(sketch, "E11.81.4", {"start": v(34.38, 20.06) * mm, "mid": v(34.1, 19.6) * mm, "end": v(33.7, 19.22) * mm});
            skLineSegment(sketch, "E11.81.5", {"start": v(32.89, 18.73) * mm, "end": v(33.7, 19.22) * mm});
            skArc(sketch, "E11.81.6", {"start": v(32.68, 18.5) * mm, "mid": v(32.77, 18.62) * mm, "end": v(32.89, 18.73) * mm});
            skArc(sketch, "E11.82.0", {"start": v(30.6, 21.77) * mm, "mid": v(30.75, 21.8) * mm, "end": v(30.9, 21.86) * mm});
            skLineSegment(sketch, "E11.82.1", {"start": v(30.9, 21.86) * mm, "end": v(31.68, 22.4) * mm});
            skArc(sketch, "E11.82.2", {"start": v(32.73, 22.65) * mm, "mid": v(32.19, 22.6) * mm, "end": v(31.68, 22.4) * mm});
            skArc(sketch, "E11.82.3", {"start": v(33, 22.24) * mm, "mid": v(32.87, 22.45) * mm, "end": v(32.73, 22.65) * mm});
            skArc(sketch, "E11.82.4", {"start": v(33, 22.24) * mm, "mid": v(32.76, 21.76) * mm, "end": v(32.4, 21.36) * mm});
            skLineSegment(sketch, "E11.82.5", {"start": v(31.6, 20.82) * mm, "end": v(32.4, 21.36) * mm});
            skArc(sketch, "E11.82.6", {"start": v(31.41, 20.57) * mm, "mid": v(31.5, 20.7) * mm, "end": v(31.6, 20.82) * mm});
            skArc(sketch, "E11.83.0", {"start": v(29.12, 23.7) * mm, "mid": v(29.27, 23.75) * mm, "end": v(29.42, 23.82) * mm});
            skLineSegment(sketch, "E11.83.1", {"start": v(29.42, 23.82) * mm, "end": v(30.17, 24.4) * mm});
            skArc(sketch, "E11.83.2", {"start": v(31.2, 24.72) * mm, "mid": v(30.66, 24.63) * mm, "end": v(30.17, 24.4) * mm});
            skArc(sketch, "E11.83.3", {"start": v(31.5, 24.33) * mm, "mid": v(31.35, 24.53) * mm, "end": v(31.2, 24.72) * mm});
            skArc(sketch, "E11.83.4", {"start": v(31.5, 24.33) * mm, "mid": v(31.28, 23.83) * mm, "end": v(30.94, 23.41) * mm});
            skLineSegment(sketch, "E11.83.5", {"start": v(30.2, 22.83) * mm, "end": v(30.94, 23.41) * mm});
            skArc(sketch, "E11.83.6", {"start": v(30.02, 22.56) * mm, "mid": v(30.1, 22.7) * mm, "end": v(30.2, 22.83) * mm});
            skArc(sketch, "E11.84.0", {"start": v(27.52, 25.54) * mm, "mid": v(27.67, 25.6) * mm, "end": v(27.81, 25.67) * mm});
            skLineSegment(sketch, "E11.84.1", {"start": v(27.81, 25.67) * mm, "end": v(28.52, 26.3) * mm});
            skArc(sketch, "E11.84.2", {"start": v(29.52, 26.69) * mm, "mid": v(29, 26.56) * mm, "end": v(28.52, 26.3) * mm});
            skArc(sketch, "E11.84.3", {"start": v(29.86, 26.32) * mm, "mid": v(29.7, 26.5) * mm, "end": v(29.52, 26.69) * mm});
            skArc(sketch, "E11.84.4", {"start": v(29.86, 26.32) * mm, "mid": v(29.67, 25.8) * mm, "end": v(29.36, 25.37) * mm});
            skLineSegment(sketch, "E11.84.5", {"start": v(28.65, 24.73) * mm, "end": v(29.36, 25.37) * mm});
            skArc(sketch, "E11.84.6", {"start": v(28.5, 24.46) * mm, "mid": v(28.56, 24.6) * mm, "end": v(28.65, 24.73) * mm});
            skArc(sketch, "E11.85.0", {"start": v(25.81, 27.27) * mm, "mid": v(25.96, 27.33) * mm, "end": v(26.1, 27.42) * mm});
            skLineSegment(sketch, "E11.85.1", {"start": v(26.1, 27.42) * mm, "end": v(26.76, 28.1) * mm});
            skArc(sketch, "E11.85.2", {"start": v(27.74, 28.54) * mm, "mid": v(27.22, 28.39) * mm, "end": v(26.76, 28.1) * mm});
            skArc(sketch, "E11.85.3", {"start": v(28.1, 28.2) * mm, "mid": v(27.91, 28.37) * mm, "end": v(27.74, 28.54) * mm});
            skArc(sketch, "E11.85.4", {"start": v(28.1, 28.2) * mm, "mid": v(27.94, 27.67) * mm, "end": v(27.66, 27.21) * mm});
            skLineSegment(sketch, "E11.85.5", {"start": v(27, 26.54) * mm, "end": v(27.66, 27.21) * mm});
            skArc(sketch, "E11.85.6", {"start": v(26.85, 26.25) * mm, "mid": v(26.9, 26.4) * mm, "end": v(27, 26.54) * mm});
            skArc(sketch, "E11.86.0", {"start": v(24, 28.89) * mm, "mid": v(24.14, 28.96) * mm, "end": v(24.27, 29.05) * mm});
            skLineSegment(sketch, "E11.86.1", {"start": v(24.27, 29.05) * mm, "end": v(24.89, 29.77) * mm});
            skArc(sketch, "E11.86.2", {"start": v(25.83, 30.28) * mm, "mid": v(25.32, 30.09) * mm, "end": v(24.89, 29.77) * mm});
            skArc(sketch, "E11.86.3", {"start": v(26.2, 29.95) * mm, "mid": v(26.02, 30.12) * mm, "end": v(25.83, 30.28) * mm});
            skArc(sketch, "E11.86.4", {"start": v(26.2, 29.95) * mm, "mid": v(26.1, 29.42) * mm, "end": v(25.84, 28.95) * mm});
            skLineSegment(sketch, "E11.86.5", {"start": v(25.22, 28.23) * mm, "end": v(25.84, 28.95) * mm});
            skArc(sketch, "E11.86.6", {"start": v(25.1, 27.93) * mm, "mid": v(25.14, 28.08) * mm, "end": v(25.22, 28.23) * mm});
            skArc(sketch, "E11.87.0", {"start": v(22.07, 30.38) * mm, "mid": v(22.21, 30.46) * mm, "end": v(22.33, 30.56) * mm});
            skLineSegment(sketch, "E11.87.1", {"start": v(22.33, 30.56) * mm, "end": v(22.9, 31.32) * mm});
            skArc(sketch, "E11.87.2", {"start": v(23.82, 31.89) * mm, "mid": v(23.32, 31.66) * mm, "end": v(22.9, 31.32) * mm});
            skArc(sketch, "E11.87.3", {"start": v(24.21, 31.59) * mm, "mid": v(24.02, 31.74) * mm, "end": v(23.82, 31.89) * mm});
            skArc(sketch, "E11.87.4", {"start": v(24.21, 31.59) * mm, "mid": v(24.13, 31.05) * mm, "end": v(23.9, 30.56) * mm});
            skLineSegment(sketch, "E11.87.5", {"start": v(23.34, 29.8) * mm, "end": v(23.9, 30.56) * mm});
            skArc(sketch, "E11.87.6", {"start": v(23.23, 29.5) * mm, "mid": v(23.27, 29.65) * mm, "end": v(23.34, 29.8) * mm});
            skArc(sketch, "E11.88.0", {"start": v(20.06, 31.74) * mm, "mid": v(20.2, 31.83) * mm, "end": v(20.3, 31.94) * mm});
            skLineSegment(sketch, "E11.88.1", {"start": v(20.3, 31.94) * mm, "end": v(20.83, 32.73) * mm});
            skArc(sketch, "E11.88.2", {"start": v(21.7, 33.36) * mm, "mid": v(21.22, 33.1) * mm, "end": v(20.83, 32.73) * mm});
            skArc(sketch, "E11.88.3", {"start": v(22.12, 33.09) * mm, "mid": v(21.91, 33.23) * mm, "end": v(21.7, 33.36) * mm});
            skArc(sketch, "E11.88.4", {"start": v(22.12, 33.09) * mm, "mid": v(22.07, 32.55) * mm, "end": v(21.88, 32.04) * mm});
            skLineSegment(sketch, "E11.88.5", {"start": v(21.36, 31.25) * mm, "end": v(21.88, 32.04) * mm});
            skArc(sketch, "E11.88.6", {"start": v(21.28, 30.94) * mm, "mid": v(21.3, 31.1) * mm, "end": v(21.36, 31.25) * mm});
            skArc(sketch, "E11.89.0", {"start": v(17.96, 32.97) * mm, "mid": v(18.09, 33.07) * mm, "end": v(18.2, 33.19) * mm});
            skLineSegment(sketch, "E11.89.1", {"start": v(18.2, 33.19) * mm, "end": v(18.67, 34.01) * mm});
            skArc(sketch, "E11.89.2", {"start": v(19.5, 34.7) * mm, "mid": v(19.04, 34.41) * mm, "end": v(18.67, 34.01) * mm});
            skArc(sketch, "E11.89.3", {"start": v(19.93, 34.45) * mm, "mid": v(19.71, 34.57) * mm, "end": v(19.5, 34.7) * mm});
            skArc(sketch, "E11.89.4", {"start": v(19.93, 34.45) * mm, "mid": v(19.92, 33.9) * mm, "end": v(19.76, 33.4) * mm});
            skLineSegment(sketch, "E11.89.5", {"start": v(19.3, 32.56) * mm, "end": v(19.76, 33.4) * mm});
            skArc(sketch, "E11.89.6", {"start": v(19.23, 32.25) * mm, "mid": v(19.25, 32.41) * mm, "end": v(19.3, 32.56) * mm});
            skArc(sketch, "E11.90.0", {"start": v(15.8, 34.07) * mm, "mid": v(15.91, 34.17) * mm, "end": v(16.01, 34.3) * mm});
            skLineSegment(sketch, "E11.90.1", {"start": v(16.01, 34.3) * mm, "end": v(16.43, 35.15) * mm});
            skArc(sketch, "E11.90.2", {"start": v(17.2, 35.89) * mm, "mid": v(16.77, 35.57) * mm, "end": v(16.43, 35.15) * mm});
            skArc(sketch, "E11.90.3", {"start": v(17.66, 35.67) * mm, "mid": v(17.43, 35.78) * mm, "end": v(17.2, 35.89) * mm});
            skArc(sketch, "E11.90.4", {"start": v(17.66, 35.67) * mm, "mid": v(17.68, 35.13) * mm, "end": v(17.56, 34.6) * mm});
            skLineSegment(sketch, "E11.90.5", {"start": v(17.14, 33.75) * mm, "end": v(17.56, 34.6) * mm});
            skArc(sketch, "E11.90.6", {"start": v(17.1, 33.43) * mm, "mid": v(17.1, 33.59) * mm, "end": v(17.14, 33.75) * mm});
            skArc(sketch, "E11.91.0", {"start": v(13.55, 35.02) * mm, "mid": v(13.67, 35.13) * mm, "end": v(13.76, 35.26) * mm});
            skLineSegment(sketch, "E11.91.1", {"start": v(13.76, 35.26) * mm, "end": v(14.12, 36.14) * mm});
            skArc(sketch, "E11.91.2", {"start": v(14.85, 36.93) * mm, "mid": v(14.43, 36.58) * mm, "end": v(14.12, 36.14) * mm});
            skArc(sketch, "E11.91.3", {"start": v(15.31, 36.74) * mm, "mid": v(15.08, 36.83) * mm, "end": v(14.85, 36.93) * mm});
            skArc(sketch, "E11.91.4", {"start": v(15.31, 36.74) * mm, "mid": v(15.37, 36.2) * mm, "end": v(15.28, 35.66) * mm});
            skLineSegment(sketch, "E11.91.5", {"start": v(14.92, 34.78) * mm, "end": v(15.28, 35.66) * mm});
            skArc(sketch, "E11.91.6", {"start": v(14.9, 34.47) * mm, "mid": v(14.9, 34.63) * mm, "end": v(14.92, 34.78) * mm});
            skArc(sketch, "E11.92.0", {"start": v(11.26, 35.82) * mm, "mid": v(11.36, 35.94) * mm, "end": v(11.45, 36.08) * mm});
            skLineSegment(sketch, "E11.92.1", {"start": v(11.45, 36.08) * mm, "end": v(11.75, 36.98) * mm});
            skArc(sketch, "E11.92.2", {"start": v(12.43, 37.8) * mm, "mid": v(12.03, 37.44) * mm, "end": v(11.75, 36.98) * mm});
            skArc(sketch, "E11.92.3", {"start": v(12.9, 37.65) * mm, "mid": v(12.67, 37.73) * mm, "end": v(12.43, 37.8) * mm});
            skArc(sketch, "E11.92.4", {"start": v(12.9, 37.65) * mm, "mid": v(13, 37.12) * mm, "end": v(12.94, 36.58) * mm});
            skLineSegment(sketch, "E11.92.5", {"start": v(12.64, 35.68) * mm, "end": v(12.94, 36.58) * mm});
            skArc(sketch, "E11.92.6", {"start": v(12.64, 35.36) * mm, "mid": v(12.63, 35.52) * mm, "end": v(12.64, 35.68) * mm});
            skArc(sketch, "E11.93.0", {"start": v(8.91, 36.48) * mm, "mid": v(9.01, 36.6) * mm, "end": v(9.09, 36.74) * mm});
            skLineSegment(sketch, "E11.93.1", {"start": v(9.09, 36.74) * mm, "end": v(9.33, 37.66) * mm});
            skArc(sketch, "E11.93.2", {"start": v(9.96, 38.53) * mm, "mid": v(9.58, 38.14) * mm, "end": v(9.33, 37.66) * mm});
            skArc(sketch, "E11.93.3", {"start": v(10.44, 38.4) * mm, "mid": v(10.2, 38.47) * mm, "end": v(9.96, 38.53) * mm});
            skArc(sketch, "E11.93.4", {"start": v(10.44, 38.4) * mm, "mid": v(10.57, 37.88) * mm, "end": v(10.55, 37.34) * mm});
            skLineSegment(sketch, "E11.93.5", {"start": v(10.3, 36.42) * mm, "end": v(10.55, 37.34) * mm});
            skArc(sketch, "E11.93.6", {"start": v(10.32, 36.1) * mm, "mid": v(10.3, 36.26) * mm, "end": v(10.3, 36.42) * mm});
            skArc(sketch, "E11.94.0", {"start": v(6.54, 36.98) * mm, "mid": v(6.62, 37.1) * mm, "end": v(6.7, 37.25) * mm});
            skLineSegment(sketch, "E11.94.1", {"start": v(6.7, 37.25) * mm, "end": v(6.87, 38.19) * mm});
            skArc(sketch, "E11.94.2", {"start": v(7.44, 39.1) * mm, "mid": v(7.1, 38.68) * mm, "end": v(6.87, 38.19) * mm});
            skArc(sketch, "E11.94.3", {"start": v(7.93, 39) * mm, "mid": v(7.69, 39.05) * mm, "end": v(7.44, 39.1) * mm});
            skArc(sketch, "E11.94.4", {"start": v(7.93, 39) * mm, "mid": v(8.1, 38.48) * mm, "end": v(8.1, 37.94) * mm});
            skLineSegment(sketch, "E11.94.5", {"start": v(7.92, 37.01) * mm, "end": v(8.1, 37.94) * mm});
            skArc(sketch, "E11.94.6", {"start": v(7.96, 36.7) * mm, "mid": v(7.93, 36.85) * mm, "end": v(7.92, 37.01) * mm});
            skArc(sketch, "E11.95.0", {"start": v(4.13, 37.32) * mm, "mid": v(4.2, 37.46) * mm, "end": v(4.27, 37.6) * mm});
            skLineSegment(sketch, "E11.95.1", {"start": v(4.27, 37.6) * mm, "end": v(4.39, 38.55) * mm});
            skArc(sketch, "E11.95.2", {"start": v(4.9, 39.5) * mm, "mid": v(4.58, 39.06) * mm, "end": v(4.39, 38.55) * mm});
            skArc(sketch, "E11.95.3", {"start": v(5.39, 39.43) * mm, "mid": v(5.14, 39.47) * mm, "end": v(4.9, 39.5) * mm});
            skArc(sketch, "E11.95.4", {"start": v(5.39, 39.43) * mm, "mid": v(5.58, 38.93) * mm, "end": v(5.63, 38.39) * mm});
            skLineSegment(sketch, "E11.95.5", {"start": v(5.51, 37.45) * mm, "end": v(5.63, 38.39) * mm});
            skArc(sketch, "E11.95.6", {"start": v(5.57, 37.13) * mm, "mid": v(5.53, 37.29) * mm, "end": v(5.51, 37.45) * mm});
            skArc(sketch, "E11.96.0", {"start": v(1.7, 37.51) * mm, "mid": v(1.77, 37.65) * mm, "end": v(1.82, 37.8) * mm});
            skLineSegment(sketch, "E11.96.1", {"start": v(1.82, 37.8) * mm, "end": v(1.88, 38.75) * mm});
            skArc(sketch, "E11.96.2", {"start": v(2.33, 39.73) * mm, "mid": v(2.04, 39.27) * mm, "end": v(1.88, 38.75) * mm});
            skArc(sketch, "E11.96.3", {"start": v(2.83, 39.7) * mm, "mid": v(2.58, 39.72) * mm, "end": v(2.33, 39.73) * mm});
            skArc(sketch, "E11.96.4", {"start": v(2.83, 39.7) * mm, "mid": v(3.05, 39.2) * mm, "end": v(3.14, 38.67) * mm});
            skLineSegment(sketch, "E11.96.5", {"start": v(3.08, 37.72) * mm, "end": v(3.14, 38.67) * mm});
            skArc(sketch, "E11.96.6", {"start": v(3.16, 37.42) * mm, "mid": v(3.1, 37.57) * mm, "end": v(3.08, 37.72) * mm});
            skArc(sketch, "E12", {"start": v(0.73, 37.54) * mm, "mid": v(1.22, 37.53) * mm, "end": v(1.7, 37.51) * mm});
            skArc(sketch, "E13.1.0", {"start": v(-1.7, 37.51) * mm, "mid": v(-1.22, 37.53) * mm, "end": v(-0.73, 37.54) * mm});
            skArc(sketch, "E13.2.0", {"start": v(-4.13, 37.32) * mm, "mid": v(-3.64, 37.37) * mm, "end": v(-3.16, 37.42) * mm});
            skArc(sketch, "E13.3.0", {"start": v(-6.54, 36.98) * mm, "mid": v(-6.05, 37.06) * mm, "end": v(-5.57, 37.13) * mm});
            skArc(sketch, "E13.4.0", {"start": v(-8.91, 36.48) * mm, "mid": v(-8.44, 36.59) * mm, "end": v(-7.96, 36.7) * mm});
            skArc(sketch, "E13.5.0", {"start": v(-11.26, 35.82) * mm, "mid": v(-10.8, 35.97) * mm, "end": v(-10.32, 36.1) * mm});
            skArc(sketch, "E13.6.0", {"start": v(-13.55, 35.02) * mm, "mid": v(-13.1, 35.2) * mm, "end": v(-12.64, 35.36) * mm});
            skArc(sketch, "E13.7.0", {"start": v(-15.8, 34.07) * mm, "mid": v(-15.35, 34.27) * mm, "end": v(-14.9, 34.47) * mm});
            skArc(sketch, "E13.8.0", {"start": v(-17.96, 32.97) * mm, "mid": v(-17.53, 33.2) * mm, "end": v(-17.1, 33.43) * mm});
            skArc(sketch, "E13.9.0", {"start": v(-20.06, 31.74) * mm, "mid": v(-19.65, 32) * mm, "end": v(-19.23, 32.25) * mm});
            skArc(sketch, "E13.10.0", {"start": v(-22.07, 30.38) * mm, "mid": v(-21.68, 30.66) * mm, "end": v(-21.28, 30.94) * mm});
            skArc(sketch, "E13.11.0", {"start": v(-24, 28.89) * mm, "mid": v(-23.62, 29.2) * mm, "end": v(-23.23, 29.5) * mm});
            skArc(sketch, "E13.12.0", {"start": v(-25.81, 27.27) * mm, "mid": v(-25.46, 27.6) * mm, "end": v(-25.1, 27.93) * mm});
            skArc(sketch, "E13.13.0", {"start": v(-27.52, 25.54) * mm, "mid": v(-27.19, 25.9) * mm, "end": v(-26.85, 26.25) * mm});
            skArc(sketch, "E13.14.0", {"start": v(-29.12, 23.7) * mm, "mid": v(-28.8, 24.08) * mm, "end": v(-28.5, 24.46) * mm});
            skArc(sketch, "E13.15.0", {"start": v(-30.6, 21.77) * mm, "mid": v(-30.3, 22.17) * mm, "end": v(-30.02, 22.56) * mm});
            skArc(sketch, "E13.16.0", {"start": v(-31.94, 19.75) * mm, "mid": v(-31.68, 20.16) * mm, "end": v(-31.41, 20.57) * mm});
            skArc(sketch, "E13.17.0", {"start": v(-33.15, 17.64) * mm, "mid": v(-32.92, 18.07) * mm, "end": v(-32.68, 18.5) * mm});
            skArc(sketch, "E13.18.0", {"start": v(-34.22, 15.46) * mm, "mid": v(-34.02, 15.9) * mm, "end": v(-33.8, 16.34) * mm});
            skArc(sketch, "E13.19.0", {"start": v(-35.15, 13.2) * mm, "mid": v(-34.98, 13.66) * mm, "end": v(-34.8, 14.12) * mm});
            skArc(sketch, "E13.20.0", {"start": v(-35.93, 10.9) * mm, "mid": v(-35.79, 11.37) * mm, "end": v(-35.64, 11.84) * mm});
            skArc(sketch, "E13.21.0", {"start": v(-36.56, 8.56) * mm, "mid": v(-36.45, 9.03) * mm, "end": v(-36.33, 9.5) * mm});
            skArc(sketch, "E13.22.0", {"start": v(-37.04, 6.17) * mm, "mid": v(-36.96, 6.65) * mm, "end": v(-36.87, 7.13) * mm});
            skArc(sketch, "E13.23.0", {"start": v(-37.36, 3.76) * mm, "mid": v(-37.3, 4.25) * mm, "end": v(-37.25, 4.73) * mm});
            skArc(sketch, "E13.24.0", {"start": v(-37.53, 1.34) * mm, "mid": v(-37.5, 1.82) * mm, "end": v(-37.48, 2.31) * mm});
            skArc(sketch, "E13.25.0", {"start": v(-37.53, -1.1) * mm, "mid": v(-37.55, -0.6) * mm, "end": v(-37.55, -0.12) * mm});
            skArc(sketch, "E13.26.0", {"start": v(-37.38, -3.52) * mm, "mid": v(-37.43, -3.04) * mm, "end": v(-37.46, -2.55) * mm});
            skArc(sketch, "E13.27.0", {"start": v(-37.08, -5.94) * mm, "mid": v(-37.15, -5.45) * mm, "end": v(-37.22, -4.97) * mm});
            skArc(sketch, "E13.28.0", {"start": v(-36.62, -8.32) * mm, "mid": v(-36.72, -7.85) * mm, "end": v(-36.82, -7.37) * mm});
            skArc(sketch, "E13.29.0", {"start": v(-36, -10.68) * mm, "mid": v(-36.14, -10.2) * mm, "end": v(-36.27, -9.74) * mm});
            skArc(sketch, "E13.30.0", {"start": v(-35.23, -12.98) * mm, "mid": v(-35.4, -12.52) * mm, "end": v(-35.56, -12.06) * mm});
            skArc(sketch, "E13.31.0", {"start": v(-34.32, -15.24) * mm, "mid": v(-34.51, -14.8) * mm, "end": v(-34.7, -14.34) * mm});
            skArc(sketch, "E13.32.0", {"start": v(-33.26, -17.43) * mm, "mid": v(-33.48, -17) * mm, "end": v(-33.7, -16.56) * mm});
            skArc(sketch, "E13.33.0", {"start": v(-32.06, -19.54) * mm, "mid": v(-32.31, -19.12) * mm, "end": v(-32.56, -18.7) * mm});
            skArc(sketch, "E13.34.0", {"start": v(-30.73, -21.58) * mm, "mid": v(-31, -21.18) * mm, "end": v(-31.28, -20.77) * mm});
            skArc(sketch, "E13.35.0", {"start": v(-29.27, -23.52) * mm, "mid": v(-29.57, -23.14) * mm, "end": v(-29.87, -22.75) * mm});
            skArc(sketch, "E13.36.0", {"start": v(-27.69, -25.37) * mm, "mid": v(-28.01, -25) * mm, "end": v(-28.34, -24.64) * mm});
            skArc(sketch, "E13.37.0", {"start": v(-25.99, -27.1) * mm, "mid": v(-26.34, -26.77) * mm, "end": v(-26.68, -26.42) * mm});
            skArc(sketch, "E13.38.0", {"start": v(-24.18, -28.73) * mm, "mid": v(-24.55, -28.41) * mm, "end": v(-24.92, -28.1) * mm});
            skArc(sketch, "E13.39.0", {"start": v(-22.27, -30.24) * mm, "mid": v(-22.66, -29.94) * mm, "end": v(-23.04, -29.65) * mm});
            skArc(sketch, "E13.40.0", {"start": v(-20.26, -31.61) * mm, "mid": v(-20.67, -31.35) * mm, "end": v(-21.08, -31.08) * mm});
            skArc(sketch, "E13.41.0", {"start": v(-18.17, -32.86) * mm, "mid": v(-18.6, -32.62) * mm, "end": v(-19.02, -32.38) * mm});
            skArc(sketch, "E13.42.0", {"start": v(-16, -33.97) * mm, "mid": v(-16.45, -33.76) * mm, "end": v(-16.89, -33.54) * mm});
            skArc(sketch, "E13.43.0", {"start": v(-13.78, -34.93) * mm, "mid": v(-14.23, -34.75) * mm, "end": v(-14.68, -34.56) * mm});
            skArc(sketch, "E13.44.0", {"start": v(-11.49, -35.75) * mm, "mid": v(-11.95, -35.6) * mm, "end": v(-12.41, -35.44) * mm});
            skArc(sketch, "E13.45.0", {"start": v(-9.15, -36.42) * mm, "mid": v(-9.62, -36.3) * mm, "end": v(-10.1, -36.17) * mm});
            skArc(sketch, "E13.46.0", {"start": v(-6.77, -36.93) * mm, "mid": v(-7.25, -36.84) * mm, "end": v(-7.73, -36.75) * mm});
            skArc(sketch, "E13.47.0", {"start": v(-4.37, -37.3) * mm, "mid": v(-4.85, -37.24) * mm, "end": v(-5.33, -37.17) * mm});
            skArc(sketch, "E13.48.0", {"start": v(-1.94, -37.5) * mm, "mid": v(-2.43, -37.47) * mm, "end": v(-2.92, -37.44) * mm});
            skArc(sketch, "E13.49.0", {"start": v(0.49, -37.55) * mm, "mid": v(0, -37.55) * mm, "end": v(-0.49, -37.55) * mm});
            skArc(sketch, "E13.50.0", {"start": v(2.92, -37.44) * mm, "mid": v(2.43, -37.47) * mm, "end": v(1.94, -37.5) * mm});
            skArc(sketch, "E13.51.0", {"start": v(5.33, -37.17) * mm, "mid": v(4.85, -37.24) * mm, "end": v(4.37, -37.3) * mm});
            skArc(sketch, "E13.52.0", {"start": v(7.73, -36.75) * mm, "mid": v(7.25, -36.84) * mm, "end": v(6.77, -36.93) * mm});
            skArc(sketch, "E13.53.0", {"start": v(10.1, -36.17) * mm, "mid": v(9.62, -36.3) * mm, "end": v(9.15, -36.42) * mm});
            skArc(sketch, "E13.54.0", {"start": v(12.41, -35.44) * mm, "mid": v(11.95, -35.6) * mm, "end": v(11.49, -35.75) * mm});
            skArc(sketch, "E13.55.0", {"start": v(14.68, -34.56) * mm, "mid": v(14.23, -34.75) * mm, "end": v(13.78, -34.93) * mm});
            skArc(sketch, "E13.56.0", {"start": v(16.89, -33.54) * mm, "mid": v(16.45, -33.76) * mm, "end": v(16, -33.97) * mm});
            skArc(sketch, "E13.57.0", {"start": v(19.02, -32.38) * mm, "mid": v(18.6, -32.62) * mm, "end": v(18.17, -32.86) * mm});
            skArc(sketch, "E13.58.0", {"start": v(21.08, -31.08) * mm, "mid": v(20.67, -31.35) * mm, "end": v(20.26, -31.61) * mm});
            skArc(sketch, "E13.59.0", {"start": v(23.04, -29.65) * mm, "mid": v(22.66, -29.94) * mm, "end": v(22.27, -30.24) * mm});
            skArc(sketch, "E13.60.0", {"start": v(24.92, -28.1) * mm, "mid": v(24.55, -28.41) * mm, "end": v(24.18, -28.73) * mm});
            skArc(sketch, "E13.61.0", {"start": v(26.68, -26.42) * mm, "mid": v(26.34, -26.77) * mm, "end": v(25.99, -27.1) * mm});
            skArc(sketch, "E13.62.0", {"start": v(28.34, -24.64) * mm, "mid": v(28.01, -25) * mm, "end": v(27.69, -25.37) * mm});
            skArc(sketch, "E13.63.0", {"start": v(29.87, -22.75) * mm, "mid": v(29.57, -23.14) * mm, "end": v(29.27, -23.52) * mm});
            skArc(sketch, "E13.64.0", {"start": v(31.28, -20.77) * mm, "mid": v(31, -21.18) * mm, "end": v(30.73, -21.58) * mm});
            skArc(sketch, "E13.65.0", {"start": v(32.56, -18.7) * mm, "mid": v(32.31, -19.12) * mm, "end": v(32.06, -19.54) * mm});
            skArc(sketch, "E13.66.0", {"start": v(33.7, -16.56) * mm, "mid": v(33.48, -17) * mm, "end": v(33.26, -17.43) * mm});
            skArc(sketch, "E13.67.0", {"start": v(34.7, -14.34) * mm, "mid": v(34.51, -14.8) * mm, "end": v(34.32, -15.24) * mm});
            skArc(sketch, "E13.68.0", {"start": v(35.56, -12.06) * mm, "mid": v(35.4, -12.52) * mm, "end": v(35.23, -12.98) * mm});
            skArc(sketch, "E13.69.0", {"start": v(36.27, -9.74) * mm, "mid": v(36.14, -10.2) * mm, "end": v(36, -10.68) * mm});
            skArc(sketch, "E13.70.0", {"start": v(36.82, -7.37) * mm, "mid": v(36.72, -7.85) * mm, "end": v(36.62, -8.32) * mm});
            skArc(sketch, "E13.71.0", {"start": v(37.22, -4.97) * mm, "mid": v(37.15, -5.45) * mm, "end": v(37.08, -5.94) * mm});
            skArc(sketch, "E13.72.0", {"start": v(37.46, -2.55) * mm, "mid": v(37.43, -3.04) * mm, "end": v(37.38, -3.52) * mm});
            skArc(sketch, "E13.73.0", {"start": v(37.55, -0.12) * mm, "mid": v(37.55, -0.6) * mm, "end": v(37.53, -1.1) * mm});
            skArc(sketch, "E13.74.0", {"start": v(37.48, 2.31) * mm, "mid": v(37.5, 1.82) * mm, "end": v(37.53, 1.34) * mm});
            skArc(sketch, "E13.75.0", {"start": v(37.25, 4.73) * mm, "mid": v(37.3, 4.25) * mm, "end": v(37.36, 3.76) * mm});
            skArc(sketch, "E13.76.0", {"start": v(36.87, 7.13) * mm, "mid": v(36.96, 6.65) * mm, "end": v(37.04, 6.17) * mm});
            skArc(sketch, "E13.77.0", {"start": v(36.33, 9.5) * mm, "mid": v(36.45, 9.03) * mm, "end": v(36.56, 8.56) * mm});
            skArc(sketch, "E13.78.0", {"start": v(35.64, 11.84) * mm, "mid": v(35.79, 11.37) * mm, "end": v(35.93, 10.9) * mm});
            skArc(sketch, "E13.79.0", {"start": v(34.8, 14.12) * mm, "mid": v(34.98, 13.66) * mm, "end": v(35.15, 13.2) * mm});
            skArc(sketch, "E13.80.0", {"start": v(33.8, 16.34) * mm, "mid": v(34.02, 15.9) * mm, "end": v(34.22, 15.46) * mm});
            skArc(sketch, "E13.81.0", {"start": v(32.68, 18.5) * mm, "mid": v(32.92, 18.07) * mm, "end": v(33.15, 17.64) * mm});
            skArc(sketch, "E13.82.0", {"start": v(31.41, 20.57) * mm, "mid": v(31.68, 20.16) * mm, "end": v(31.94, 19.75) * mm});
            skArc(sketch, "E13.83.0", {"start": v(30.02, 22.56) * mm, "mid": v(30.3, 22.17) * mm, "end": v(30.6, 21.77) * mm});
            skArc(sketch, "E13.84.0", {"start": v(28.5, 24.46) * mm, "mid": v(28.8, 24.08) * mm, "end": v(29.12, 23.7) * mm});
            skArc(sketch, "E13.85.0", {"start": v(26.85, 26.25) * mm, "mid": v(27.19, 25.9) * mm, "end": v(27.52, 25.54) * mm});
            skArc(sketch, "E13.86.0", {"start": v(25.1, 27.93) * mm, "mid": v(25.46, 27.6) * mm, "end": v(25.81, 27.27) * mm});
            skArc(sketch, "E13.87.0", {"start": v(23.23, 29.5) * mm, "mid": v(23.62, 29.2) * mm, "end": v(24, 28.89) * mm});
            skArc(sketch, "E13.88.0", {"start": v(21.28, 30.94) * mm, "mid": v(21.68, 30.66) * mm, "end": v(22.07, 30.38) * mm});
            skArc(sketch, "E13.89.0", {"start": v(19.23, 32.25) * mm, "mid": v(19.65, 32) * mm, "end": v(20.06, 31.74) * mm});
            skArc(sketch, "E13.90.0", {"start": v(17.1, 33.43) * mm, "mid": v(17.53, 33.2) * mm, "end": v(17.96, 32.97) * mm});
            skArc(sketch, "E13.91.0", {"start": v(14.9, 34.47) * mm, "mid": v(15.35, 34.27) * mm, "end": v(15.8, 34.07) * mm});
            skArc(sketch, "E13.92.0", {"start": v(12.64, 35.36) * mm, "mid": v(13.1, 35.2) * mm, "end": v(13.55, 35.02) * mm});
            skArc(sketch, "E13.93.0", {"start": v(10.32, 36.1) * mm, "mid": v(10.8, 35.97) * mm, "end": v(11.26, 35.82) * mm});
            skArc(sketch, "E13.94.0", {"start": v(7.96, 36.7) * mm, "mid": v(8.44, 36.59) * mm, "end": v(8.91, 36.48) * mm});
            skArc(sketch, "E13.95.0", {"start": v(5.57, 37.13) * mm, "mid": v(6.05, 37.06) * mm, "end": v(6.54, 36.98) * mm});
            skArc(sketch, "E13.96.0", {"start": v(3.16, 37.42) * mm, "mid": v(3.64, 37.37) * mm, "end": v(4.13, 37.32) * mm});
            skCircle(sketch, "E14", {"center": v(0, 0) * mm, "radius": 3.5 * mm});
            skSolve(sketch);
        }
        {
            var Q0;
            Q0 = qSketchRegion(id + "F0", true);
            extrude(context, id + "F1", {"entities" : qUnion([Q0]), "depth" : 6 * mm, "offsetDistance" : 25 * mm});
        }
        {
            var Q0;
            Q0=qCreatedBy(makeId("Top.planeOp"),FACE);
            var sketch = newSketch(context, id + "F2", { "sketchPlane" : qUnion([Q0])});
            skArc(sketch, "E15", {"start": v(0.25, 12.2) * mm, "mid": v(0, 12.2) * mm, "end": v(-0.25, 12.2) * mm});
            skCircle(sketch, "E16", {"center": v(0, 0) * mm, "radius": 11.2 * mm, "construction": true});
            skArc(sketch, "E17", {"start": v(-0.63, 9.93) * mm, "mid": v(-0.68, 9.93) * mm, "end": v(-0.73, 9.92) * mm});
            skCircle(sketch, "E18", {"center": v(0, 0) * mm, "radius": 3.5 * mm});
            skArc(sketch, "E19", {"start": v(-0.25, 12.2) * mm, "mid": v(-0.5, 11.72) * mm, "end": v(-0.63, 11.18) * mm});
            skArc(sketch, "E20", {"start": v(-0.73, 9.92) * mm, "mid": v(-0.67, 10.07) * mm, "end": v(-0.63, 10.23) * mm});
            skLineSegment(sketch, "E21", {"start": v(-0.63, 10.23) * mm, "end": v(-0.63, 11.18) * mm});
            skArc(sketch, "E22.MirrorCS", {"start": v(0.25, 12.2) * mm, "mid": v(0.5, 11.72) * mm, "end": v(0.63, 11.18) * mm});
            skLineSegment(sketch, "E23.MirrorCS", {"start": v(0.63, 10.23) * mm, "end": v(0.63, 11.18) * mm});
            skArc(sketch, "E24.MirrorCS", {"start": v(0.73, 9.92) * mm, "mid": v(0.67, 10.07) * mm, "end": v(0.63, 10.23) * mm});
            skArc(sketch, "E25.1.0", {"start": v(-2.92, 9.51) * mm, "mid": v(-2.9, 9.67) * mm, "end": v(-2.89, 9.83) * mm});
            skLineSegment(sketch, "E25.1.1", {"start": v(-2.89, 9.83) * mm, "end": v(-3.1, 10.76) * mm});
            skArc(sketch, "E25.1.2", {"start": v(-2.96, 11.84) * mm, "mid": v(-3.1, 11.3) * mm, "end": v(-3.1, 10.76) * mm});
            skArc(sketch, "E25.1.3", {"start": v(-2.47, 11.95) * mm, "mid": v(-2.71, 11.9) * mm, "end": v(-2.96, 11.84) * mm});
            skArc(sketch, "E25.1.4", {"start": v(-2.47, 11.95) * mm, "mid": v(-2.11, 11.54) * mm, "end": v(-1.88, 11.04) * mm});
            skLineSegment(sketch, "E25.1.5", {"start": v(-1.66, 10.11) * mm, "end": v(-1.88, 11.04) * mm});
            skArc(sketch, "E25.1.6", {"start": v(-1.5, 9.84) * mm, "mid": v(-1.6, 9.97) * mm, "end": v(-1.66, 10.11) * mm});
            skArc(sketch, "E25.2.0", {"start": v(-4.96, 8.62) * mm, "mid": v(-4.97, 8.79) * mm, "end": v(-5, 8.94) * mm});
            skLineSegment(sketch, "E25.2.1", {"start": v(-5, 8.94) * mm, "end": v(-5.42, 9.8) * mm});
            skArc(sketch, "E25.2.2", {"start": v(-5.52, 10.88) * mm, "mid": v(-5.54, 10.33) * mm, "end": v(-5.42, 9.8) * mm});
            skArc(sketch, "E25.2.3", {"start": v(-5.07, 11.1) * mm, "mid": v(-5.3, 11) * mm, "end": v(-5.52, 10.88) * mm});
            skArc(sketch, "E25.2.4", {"start": v(-5.07, 11.1) * mm, "mid": v(-4.62, 10.78) * mm, "end": v(-4.29, 10.35) * mm});
            skLineSegment(sketch, "E25.2.5", {"start": v(-3.87, 9.49) * mm, "end": v(-4.29, 10.35) * mm});
            skArc(sketch, "E25.2.6", {"start": v(-3.65, 9.26) * mm, "mid": v(-3.77, 9.36) * mm, "end": v(-3.87, 9.49) * mm});
            skArc(sketch, "E25.3.0", {"start": v(-6.76, 7.3) * mm, "mid": v(-6.8, 7.46) * mm, "end": v(-6.87, 7.6) * mm});
            skLineSegment(sketch, "E25.3.1", {"start": v(-6.87, 7.6) * mm, "end": v(-7.46, 8.35) * mm});
            skArc(sketch, "E25.3.2", {"start": v(-7.8, 9.38) * mm, "mid": v(-7.7, 8.84) * mm, "end": v(-7.46, 8.35) * mm});
            skArc(sketch, "E25.3.3", {"start": v(-7.4, 9.7) * mm, "mid": v(-7.6, 9.54) * mm, "end": v(-7.8, 9.38) * mm});
            skArc(sketch, "E25.3.4", {"start": v(-7.4, 9.7) * mm, "mid": v(-6.9, 9.48) * mm, "end": v(-6.48, 9.13) * mm});
            skLineSegment(sketch, "E25.3.5", {"start": v(-5.89, 8.39) * mm, "end": v(-6.48, 9.13) * mm});
            skArc(sketch, "E25.3.6", {"start": v(-5.62, 8.21) * mm, "mid": v(-5.76, 8.3) * mm, "end": v(-5.89, 8.39) * mm});
            skArc(sketch, "E25.4.0", {"start": v(-8.21, 5.62) * mm, "mid": v(-8.3, 5.76) * mm, "end": v(-8.39, 5.89) * mm});
            skLineSegment(sketch, "E25.4.1", {"start": v(-8.39, 5.89) * mm, "end": v(-9.13, 6.48) * mm});
            skArc(sketch, "E25.4.2", {"start": v(-9.7, 7.4) * mm, "mid": v(-9.48, 6.9) * mm, "end": v(-9.13, 6.48) * mm});
            skArc(sketch, "E25.4.3", {"start": v(-9.38, 7.8) * mm, "mid": v(-9.54, 7.6) * mm, "end": v(-9.7, 7.4) * mm});
            skArc(sketch, "E25.4.4", {"start": v(-9.38, 7.8) * mm, "mid": v(-8.84, 7.7) * mm, "end": v(-8.35, 7.46) * mm});
            skLineSegment(sketch, "E25.4.5", {"start": v(-7.6, 6.87) * mm, "end": v(-8.35, 7.46) * mm});
            skArc(sketch, "E25.4.6", {"start": v(-7.3, 6.76) * mm, "mid": v(-7.46, 6.8) * mm, "end": v(-7.6, 6.87) * mm});
            skArc(sketch, "E25.5.0", {"start": v(-9.26, 3.65) * mm, "mid": v(-9.36, 3.77) * mm, "end": v(-9.49, 3.87) * mm});
            skLineSegment(sketch, "E25.5.1", {"start": v(-9.49, 3.87) * mm, "end": v(-10.35, 4.29) * mm});
            skArc(sketch, "E25.5.2", {"start": v(-11.1, 5.07) * mm, "mid": v(-10.78, 4.62) * mm, "end": v(-10.35, 4.29) * mm});
            skArc(sketch, "E25.5.3", {"start": v(-10.88, 5.52) * mm, "mid": v(-11, 5.3) * mm, "end": v(-11.1, 5.07) * mm});
            skArc(sketch, "E25.5.4", {"start": v(-10.88, 5.52) * mm, "mid": v(-10.33, 5.54) * mm, "end": v(-9.8, 5.42) * mm});
            skLineSegment(sketch, "E25.5.5", {"start": v(-8.94, 5) * mm, "end": v(-9.8, 5.42) * mm});
            skArc(sketch, "E25.5.6", {"start": v(-8.62, 4.96) * mm, "mid": v(-8.79, 4.97) * mm, "end": v(-8.94, 5) * mm});
            skArc(sketch, "E25.6.0", {"start": v(-9.84, 1.5) * mm, "mid": v(-9.97, 1.6) * mm, "end": v(-10.11, 1.66) * mm});
            skLineSegment(sketch, "E25.6.1", {"start": v(-10.11, 1.66) * mm, "end": v(-11.04, 1.88) * mm});
            skArc(sketch, "E25.6.2", {"start": v(-11.95, 2.47) * mm, "mid": v(-11.54, 2.11) * mm, "end": v(-11.04, 1.88) * mm});
            skArc(sketch, "E25.6.3", {"start": v(-11.84, 2.96) * mm, "mid": v(-11.9, 2.71) * mm, "end": v(-11.95, 2.47) * mm});
            skArc(sketch, "E25.6.4", {"start": v(-11.84, 2.96) * mm, "mid": v(-11.3, 3.1) * mm, "end": v(-10.76, 3.1) * mm});
            skLineSegment(sketch, "E25.6.5", {"start": v(-9.83, 2.89) * mm, "end": v(-10.76, 3.1) * mm});
            skArc(sketch, "E25.6.6", {"start": v(-9.51, 2.92) * mm, "mid": v(-9.67, 2.9) * mm, "end": v(-9.83, 2.89) * mm});
            skArc(sketch, "E25.7.0", {"start": v(-9.92, -0.73) * mm, "mid": v(-10.07, -0.67) * mm, "end": v(-10.23, -0.63) * mm});
            skLineSegment(sketch, "E25.7.1", {"start": v(-10.23, -0.63) * mm, "end": v(-11.18, -0.63) * mm});
            skArc(sketch, "E25.7.2", {"start": v(-12.2, -0.25) * mm, "mid": v(-11.72, -0.5) * mm, "end": v(-11.18, -0.63) * mm});
            skArc(sketch, "E25.7.3", {"start": v(-12.2, 0.25) * mm, "mid": v(-12.2, 0) * mm, "end": v(-12.2, -0.25) * mm});
            skArc(sketch, "E25.7.4", {"start": v(-12.2, 0.25) * mm, "mid": v(-11.72, 0.5) * mm, "end": v(-11.18, 0.63) * mm});
            skLineSegment(sketch, "E25.7.5", {"start": v(-10.23, 0.63) * mm, "end": v(-11.18, 0.63) * mm});
            skArc(sketch, "E25.7.6", {"start": v(-9.92, 0.73) * mm, "mid": v(-10.07, 0.67) * mm, "end": v(-10.23, 0.63) * mm});
            skArc(sketch, "E25.8.0", {"start": v(-9.51, -2.92) * mm, "mid": v(-9.67, -2.9) * mm, "end": v(-9.83, -2.89) * mm});
            skLineSegment(sketch, "E25.8.1", {"start": v(-9.83, -2.89) * mm, "end": v(-10.76, -3.1) * mm});
            skArc(sketch, "E25.8.2", {"start": v(-11.84, -2.96) * mm, "mid": v(-11.3, -3.1) * mm, "end": v(-10.76, -3.1) * mm});
            skArc(sketch, "E25.8.3", {"start": v(-11.95, -2.47) * mm, "mid": v(-11.9, -2.71) * mm, "end": v(-11.84, -2.96) * mm});
            skArc(sketch, "E25.8.4", {"start": v(-11.95, -2.47) * mm, "mid": v(-11.54, -2.11) * mm, "end": v(-11.04, -1.88) * mm});
            skLineSegment(sketch, "E25.8.5", {"start": v(-10.11, -1.66) * mm, "end": v(-11.04, -1.88) * mm});
            skArc(sketch, "E25.8.6", {"start": v(-9.84, -1.5) * mm, "mid": v(-9.97, -1.6) * mm, "end": v(-10.11, -1.66) * mm});
            skArc(sketch, "E25.9.0", {"start": v(-8.62, -4.96) * mm, "mid": v(-8.79, -4.97) * mm, "end": v(-8.94, -5) * mm});
            skLineSegment(sketch, "E25.9.1", {"start": v(-8.94, -5) * mm, "end": v(-9.8, -5.42) * mm});
            skArc(sketch, "E25.9.2", {"start": v(-10.88, -5.52) * mm, "mid": v(-10.33, -5.54) * mm, "end": v(-9.8, -5.42) * mm});
            skArc(sketch, "E25.9.3", {"start": v(-11.1, -5.07) * mm, "mid": v(-11, -5.3) * mm, "end": v(-10.88, -5.52) * mm});
            skArc(sketch, "E25.9.4", {"start": v(-11.1, -5.07) * mm, "mid": v(-10.78, -4.62) * mm, "end": v(-10.35, -4.29) * mm});
            skLineSegment(sketch, "E25.9.5", {"start": v(-9.49, -3.87) * mm, "end": v(-10.35, -4.29) * mm});
            skArc(sketch, "E25.9.6", {"start": v(-9.26, -3.65) * mm, "mid": v(-9.36, -3.77) * mm, "end": v(-9.49, -3.87) * mm});
            skArc(sketch, "E25.10.0", {"start": v(-7.3, -6.76) * mm, "mid": v(-7.46, -6.8) * mm, "end": v(-7.6, -6.87) * mm});
            skLineSegment(sketch, "E25.10.1", {"start": v(-7.6, -6.87) * mm, "end": v(-8.35, -7.46) * mm});
            skArc(sketch, "E25.10.2", {"start": v(-9.38, -7.8) * mm, "mid": v(-8.84, -7.7) * mm, "end": v(-8.35, -7.46) * mm});
            skArc(sketch, "E25.10.3", {"start": v(-9.7, -7.4) * mm, "mid": v(-9.54, -7.6) * mm, "end": v(-9.38, -7.8) * mm});
            skArc(sketch, "E25.10.4", {"start": v(-9.7, -7.4) * mm, "mid": v(-9.48, -6.9) * mm, "end": v(-9.13, -6.48) * mm});
            skLineSegment(sketch, "E25.10.5", {"start": v(-8.39, -5.89) * mm, "end": v(-9.13, -6.48) * mm});
            skArc(sketch, "E25.10.6", {"start": v(-8.21, -5.62) * mm, "mid": v(-8.3, -5.76) * mm, "end": v(-8.39, -5.89) * mm});
            skArc(sketch, "E25.11.0", {"start": v(-5.62, -8.21) * mm, "mid": v(-5.76, -8.3) * mm, "end": v(-5.89, -8.39) * mm});
            skLineSegment(sketch, "E25.11.1", {"start": v(-5.89, -8.39) * mm, "end": v(-6.48, -9.13) * mm});
            skArc(sketch, "E25.11.2", {"start": v(-7.4, -9.7) * mm, "mid": v(-6.9, -9.48) * mm, "end": v(-6.48, -9.13) * mm});
            skArc(sketch, "E25.11.3", {"start": v(-7.8, -9.38) * mm, "mid": v(-7.6, -9.54) * mm, "end": v(-7.4, -9.7) * mm});
            skArc(sketch, "E25.11.4", {"start": v(-7.8, -9.38) * mm, "mid": v(-7.7, -8.84) * mm, "end": v(-7.46, -8.35) * mm});
            skLineSegment(sketch, "E25.11.5", {"start": v(-6.87, -7.6) * mm, "end": v(-7.46, -8.35) * mm});
            skArc(sketch, "E25.11.6", {"start": v(-6.76, -7.3) * mm, "mid": v(-6.8, -7.46) * mm, "end": v(-6.87, -7.6) * mm});
            skArc(sketch, "E25.12.0", {"start": v(-3.65, -9.26) * mm, "mid": v(-3.77, -9.36) * mm, "end": v(-3.87, -9.49) * mm});
            skLineSegment(sketch, "E25.12.1", {"start": v(-3.87, -9.49) * mm, "end": v(-4.29, -10.35) * mm});
            skArc(sketch, "E25.12.2", {"start": v(-5.07, -11.1) * mm, "mid": v(-4.62, -10.78) * mm, "end": v(-4.29, -10.35) * mm});
            skArc(sketch, "E25.12.3", {"start": v(-5.52, -10.88) * mm, "mid": v(-5.3, -11) * mm, "end": v(-5.07, -11.1) * mm});
            skArc(sketch, "E25.12.4", {"start": v(-5.52, -10.88) * mm, "mid": v(-5.54, -10.33) * mm, "end": v(-5.42, -9.8) * mm});
            skLineSegment(sketch, "E25.12.5", {"start": v(-5, -8.94) * mm, "end": v(-5.42, -9.8) * mm});
            skArc(sketch, "E25.12.6", {"start": v(-4.96, -8.62) * mm, "mid": v(-4.97, -8.79) * mm, "end": v(-5, -8.94) * mm});
            skArc(sketch, "E25.13.0", {"start": v(-1.5, -9.84) * mm, "mid": v(-1.6, -9.97) * mm, "end": v(-1.66, -10.11) * mm});
            skLineSegment(sketch, "E25.13.1", {"start": v(-1.66, -10.11) * mm, "end": v(-1.88, -11.04) * mm});
            skArc(sketch, "E25.13.2", {"start": v(-2.47, -11.95) * mm, "mid": v(-2.11, -11.54) * mm, "end": v(-1.88, -11.04) * mm});
            skArc(sketch, "E25.13.3", {"start": v(-2.96, -11.84) * mm, "mid": v(-2.71, -11.9) * mm, "end": v(-2.47, -11.95) * mm});
            skArc(sketch, "E25.13.4", {"start": v(-2.96, -11.84) * mm, "mid": v(-3.1, -11.3) * mm, "end": v(-3.1, -10.76) * mm});
            skLineSegment(sketch, "E25.13.5", {"start": v(-2.89, -9.83) * mm, "end": v(-3.1, -10.76) * mm});
            skArc(sketch, "E25.13.6", {"start": v(-2.92, -9.51) * mm, "mid": v(-2.9, -9.67) * mm, "end": v(-2.89, -9.83) * mm});
            skArc(sketch, "E25.14.0", {"start": v(0.73, -9.92) * mm, "mid": v(0.67, -10.07) * mm, "end": v(0.63, -10.23) * mm});
            skLineSegment(sketch, "E25.14.1", {"start": v(0.63, -10.23) * mm, "end": v(0.63, -11.18) * mm});
            skArc(sketch, "E25.14.2", {"start": v(0.25, -12.2) * mm, "mid": v(0.5, -11.72) * mm, "end": v(0.63, -11.18) * mm});
            skArc(sketch, "E25.14.3", {"start": v(-0.25, -12.2) * mm, "mid": v(0, -12.2) * mm, "end": v(0.25, -12.2) * mm});
            skArc(sketch, "E25.14.4", {"start": v(-0.25, -12.2) * mm, "mid": v(-0.5, -11.72) * mm, "end": v(-0.63, -11.18) * mm});
            skLineSegment(sketch, "E25.14.5", {"start": v(-0.63, -10.23) * mm, "end": v(-0.63, -11.18) * mm});
            skArc(sketch, "E25.14.6", {"start": v(-0.73, -9.92) * mm, "mid": v(-0.67, -10.07) * mm, "end": v(-0.63, -10.23) * mm});
            skArc(sketch, "E25.15.0", {"start": v(2.92, -9.51) * mm, "mid": v(2.9, -9.67) * mm, "end": v(2.89, -9.83) * mm});
            skLineSegment(sketch, "E25.15.1", {"start": v(2.89, -9.83) * mm, "end": v(3.1, -10.76) * mm});
            skArc(sketch, "E25.15.2", {"start": v(2.96, -11.84) * mm, "mid": v(3.1, -11.3) * mm, "end": v(3.1, -10.76) * mm});
            skArc(sketch, "E25.15.3", {"start": v(2.47, -11.95) * mm, "mid": v(2.71, -11.9) * mm, "end": v(2.96, -11.84) * mm});
            skArc(sketch, "E25.15.4", {"start": v(2.47, -11.95) * mm, "mid": v(2.11, -11.54) * mm, "end": v(1.88, -11.04) * mm});
            skLineSegment(sketch, "E25.15.5", {"start": v(1.66, -10.11) * mm, "end": v(1.88, -11.04) * mm});
            skArc(sketch, "E25.15.6", {"start": v(1.5, -9.84) * mm, "mid": v(1.6, -9.97) * mm, "end": v(1.66, -10.11) * mm});
            skArc(sketch, "E25.16.0", {"start": v(4.96, -8.62) * mm, "mid": v(4.97, -8.79) * mm, "end": v(5, -8.94) * mm});
            skLineSegment(sketch, "E25.16.1", {"start": v(5, -8.94) * mm, "end": v(5.42, -9.8) * mm});
            skArc(sketch, "E25.16.2", {"start": v(5.52, -10.88) * mm, "mid": v(5.54, -10.33) * mm, "end": v(5.42, -9.8) * mm});
            skArc(sketch, "E25.16.3", {"start": v(5.07, -11.1) * mm, "mid": v(5.3, -11) * mm, "end": v(5.52, -10.88) * mm});
            skArc(sketch, "E25.16.4", {"start": v(5.07, -11.1) * mm, "mid": v(4.62, -10.78) * mm, "end": v(4.29, -10.35) * mm});
            skLineSegment(sketch, "E25.16.5", {"start": v(3.87, -9.49) * mm, "end": v(4.29, -10.35) * mm});
            skArc(sketch, "E25.16.6", {"start": v(3.65, -9.26) * mm, "mid": v(3.77, -9.36) * mm, "end": v(3.87, -9.49) * mm});
            skArc(sketch, "E25.17.0", {"start": v(6.76, -7.3) * mm, "mid": v(6.8, -7.46) * mm, "end": v(6.87, -7.6) * mm});
            skLineSegment(sketch, "E25.17.1", {"start": v(6.87, -7.6) * mm, "end": v(7.46, -8.35) * mm});
            skArc(sketch, "E25.17.2", {"start": v(7.8, -9.38) * mm, "mid": v(7.7, -8.84) * mm, "end": v(7.46, -8.35) * mm});
            skArc(sketch, "E25.17.3", {"start": v(7.4, -9.7) * mm, "mid": v(7.6, -9.54) * mm, "end": v(7.8, -9.38) * mm});
            skArc(sketch, "E25.17.4", {"start": v(7.4, -9.7) * mm, "mid": v(6.9, -9.48) * mm, "end": v(6.48, -9.13) * mm});
            skLineSegment(sketch, "E25.17.5", {"start": v(5.89, -8.39) * mm, "end": v(6.48, -9.13) * mm});
            skArc(sketch, "E25.17.6", {"start": v(5.62, -8.21) * mm, "mid": v(5.76, -8.3) * mm, "end": v(5.89, -8.39) * mm});
            skArc(sketch, "E25.18.0", {"start": v(8.21, -5.62) * mm, "mid": v(8.3, -5.76) * mm, "end": v(8.39, -5.89) * mm});
            skLineSegment(sketch, "E25.18.1", {"start": v(8.39, -5.89) * mm, "end": v(9.13, -6.48) * mm});
            skArc(sketch, "E25.18.2", {"start": v(9.7, -7.4) * mm, "mid": v(9.48, -6.9) * mm, "end": v(9.13, -6.48) * mm});
            skArc(sketch, "E25.18.3", {"start": v(9.38, -7.8) * mm, "mid": v(9.54, -7.6) * mm, "end": v(9.7, -7.4) * mm});
            skArc(sketch, "E25.18.4", {"start": v(9.38, -7.8) * mm, "mid": v(8.84, -7.7) * mm, "end": v(8.35, -7.46) * mm});
            skLineSegment(sketch, "E25.18.5", {"start": v(7.6, -6.87) * mm, "end": v(8.35, -7.46) * mm});
            skArc(sketch, "E25.18.6", {"start": v(7.3, -6.76) * mm, "mid": v(7.46, -6.8) * mm, "end": v(7.6, -6.87) * mm});
            skArc(sketch, "E25.19.0", {"start": v(9.26, -3.65) * mm, "mid": v(9.36, -3.77) * mm, "end": v(9.49, -3.87) * mm});
            skLineSegment(sketch, "E25.19.1", {"start": v(9.49, -3.87) * mm, "end": v(10.35, -4.29) * mm});
            skArc(sketch, "E25.19.2", {"start": v(11.1, -5.07) * mm, "mid": v(10.78, -4.62) * mm, "end": v(10.35, -4.29) * mm});
            skArc(sketch, "E25.19.3", {"start": v(10.88, -5.52) * mm, "mid": v(11, -5.3) * mm, "end": v(11.1, -5.07) * mm});
            skArc(sketch, "E25.19.4", {"start": v(10.88, -5.52) * mm, "mid": v(10.33, -5.54) * mm, "end": v(9.8, -5.42) * mm});
            skLineSegment(sketch, "E25.19.5", {"start": v(8.94, -5) * mm, "end": v(9.8, -5.42) * mm});
            skArc(sketch, "E25.19.6", {"start": v(8.62, -4.96) * mm, "mid": v(8.79, -4.97) * mm, "end": v(8.94, -5) * mm});
            skArc(sketch, "E25.20.0", {"start": v(9.84, -1.5) * mm, "mid": v(9.97, -1.6) * mm, "end": v(10.11, -1.66) * mm});
            skLineSegment(sketch, "E25.20.1", {"start": v(10.11, -1.66) * mm, "end": v(11.04, -1.88) * mm});
            skArc(sketch, "E25.20.2", {"start": v(11.95, -2.47) * mm, "mid": v(11.54, -2.11) * mm, "end": v(11.04, -1.88) * mm});
            skArc(sketch, "E25.20.3", {"start": v(11.84, -2.96) * mm, "mid": v(11.9, -2.71) * mm, "end": v(11.95, -2.47) * mm});
            skArc(sketch, "E25.20.4", {"start": v(11.84, -2.96) * mm, "mid": v(11.3, -3.1) * mm, "end": v(10.76, -3.1) * mm});
            skLineSegment(sketch, "E25.20.5", {"start": v(9.83, -2.89) * mm, "end": v(10.76, -3.1) * mm});
            skArc(sketch, "E25.20.6", {"start": v(9.51, -2.92) * mm, "mid": v(9.67, -2.9) * mm, "end": v(9.83, -2.89) * mm});
            skArc(sketch, "E25.21.0", {"start": v(9.92, 0.73) * mm, "mid": v(10.07, 0.67) * mm, "end": v(10.23, 0.63) * mm});
            skLineSegment(sketch, "E25.21.1", {"start": v(10.23, 0.63) * mm, "end": v(11.18, 0.63) * mm});
            skArc(sketch, "E25.21.2", {"start": v(12.2, 0.25) * mm, "mid": v(11.72, 0.5) * mm, "end": v(11.18, 0.63) * mm});
            skArc(sketch, "E25.21.3", {"start": v(12.2, -0.25) * mm, "mid": v(12.2, 0) * mm, "end": v(12.2, 0.25) * mm});
            skArc(sketch, "E25.21.4", {"start": v(12.2, -0.25) * mm, "mid": v(11.72, -0.5) * mm, "end": v(11.18, -0.63) * mm});
            skLineSegment(sketch, "E25.21.5", {"start": v(10.23, -0.63) * mm, "end": v(11.18, -0.63) * mm});
            skArc(sketch, "E25.21.6", {"start": v(9.92, -0.73) * mm, "mid": v(10.07, -0.67) * mm, "end": v(10.23, -0.63) * mm});
            skArc(sketch, "E25.22.0", {"start": v(9.51, 2.92) * mm, "mid": v(9.67, 2.9) * mm, "end": v(9.83, 2.89) * mm});
            skLineSegment(sketch, "E25.22.1", {"start": v(9.83, 2.89) * mm, "end": v(10.76, 3.1) * mm});
            skArc(sketch, "E25.22.2", {"start": v(11.84, 2.96) * mm, "mid": v(11.3, 3.1) * mm, "end": v(10.76, 3.1) * mm});
            skArc(sketch, "E25.22.3", {"start": v(11.95, 2.47) * mm, "mid": v(11.9, 2.71) * mm, "end": v(11.84, 2.96) * mm});
            skArc(sketch, "E25.22.4", {"start": v(11.95, 2.47) * mm, "mid": v(11.54, 2.11) * mm, "end": v(11.04, 1.88) * mm});
            skLineSegment(sketch, "E25.22.5", {"start": v(10.11, 1.66) * mm, "end": v(11.04, 1.88) * mm});
            skArc(sketch, "E25.22.6", {"start": v(9.84, 1.5) * mm, "mid": v(9.97, 1.6) * mm, "end": v(10.11, 1.66) * mm});
            skArc(sketch, "E25.23.0", {"start": v(8.62, 4.96) * mm, "mid": v(8.79, 4.97) * mm, "end": v(8.94, 5) * mm});
            skLineSegment(sketch, "E25.23.1", {"start": v(8.94, 5) * mm, "end": v(9.8, 5.42) * mm});
            skArc(sketch, "E25.23.2", {"start": v(10.88, 5.52) * mm, "mid": v(10.33, 5.54) * mm, "end": v(9.8, 5.42) * mm});
            skArc(sketch, "E25.23.3", {"start": v(11.1, 5.07) * mm, "mid": v(11, 5.3) * mm, "end": v(10.88, 5.52) * mm});
            skArc(sketch, "E25.23.4", {"start": v(11.1, 5.07) * mm, "mid": v(10.78, 4.62) * mm, "end": v(10.35, 4.29) * mm});
            skLineSegment(sketch, "E25.23.5", {"start": v(9.49, 3.87) * mm, "end": v(10.35, 4.29) * mm});
            skArc(sketch, "E25.23.6", {"start": v(9.26, 3.65) * mm, "mid": v(9.36, 3.77) * mm, "end": v(9.49, 3.87) * mm});
            skArc(sketch, "E25.24.0", {"start": v(7.3, 6.76) * mm, "mid": v(7.46, 6.8) * mm, "end": v(7.6, 6.87) * mm});
            skLineSegment(sketch, "E25.24.1", {"start": v(7.6, 6.87) * mm, "end": v(8.35, 7.46) * mm});
            skArc(sketch, "E25.24.2", {"start": v(9.38, 7.8) * mm, "mid": v(8.84, 7.7) * mm, "end": v(8.35, 7.46) * mm});
            skArc(sketch, "E25.24.3", {"start": v(9.7, 7.4) * mm, "mid": v(9.54, 7.6) * mm, "end": v(9.38, 7.8) * mm});
            skArc(sketch, "E25.24.4", {"start": v(9.7, 7.4) * mm, "mid": v(9.48, 6.9) * mm, "end": v(9.13, 6.48) * mm});
            skLineSegment(sketch, "E25.24.5", {"start": v(8.39, 5.89) * mm, "end": v(9.13, 6.48) * mm});
            skArc(sketch, "E25.24.6", {"start": v(8.21, 5.62) * mm, "mid": v(8.3, 5.76) * mm, "end": v(8.39, 5.89) * mm});
            skArc(sketch, "E25.25.0", {"start": v(5.62, 8.21) * mm, "mid": v(5.76, 8.3) * mm, "end": v(5.89, 8.39) * mm});
            skLineSegment(sketch, "E25.25.1", {"start": v(5.89, 8.39) * mm, "end": v(6.48, 9.13) * mm});
            skArc(sketch, "E25.25.2", {"start": v(7.4, 9.7) * mm, "mid": v(6.9, 9.48) * mm, "end": v(6.48, 9.13) * mm});
            skArc(sketch, "E25.25.3", {"start": v(7.8, 9.38) * mm, "mid": v(7.6, 9.54) * mm, "end": v(7.4, 9.7) * mm});
            skArc(sketch, "E25.25.4", {"start": v(7.8, 9.38) * mm, "mid": v(7.7, 8.84) * mm, "end": v(7.46, 8.35) * mm});
            skLineSegment(sketch, "E25.25.5", {"start": v(6.87, 7.6) * mm, "end": v(7.46, 8.35) * mm});
            skArc(sketch, "E25.25.6", {"start": v(6.76, 7.3) * mm, "mid": v(6.8, 7.46) * mm, "end": v(6.87, 7.6) * mm});
            skArc(sketch, "E25.26.0", {"start": v(3.65, 9.26) * mm, "mid": v(3.77, 9.36) * mm, "end": v(3.87, 9.49) * mm});
            skLineSegment(sketch, "E25.26.1", {"start": v(3.87, 9.49) * mm, "end": v(4.29, 10.35) * mm});
            skArc(sketch, "E25.26.2", {"start": v(5.07, 11.1) * mm, "mid": v(4.62, 10.78) * mm, "end": v(4.29, 10.35) * mm});
            skArc(sketch, "E25.26.3", {"start": v(5.52, 10.88) * mm, "mid": v(5.3, 11) * mm, "end": v(5.07, 11.1) * mm});
            skArc(sketch, "E25.26.4", {"start": v(5.52, 10.88) * mm, "mid": v(5.54, 10.33) * mm, "end": v(5.42, 9.8) * mm});
            skLineSegment(sketch, "E25.26.5", {"start": v(5, 8.94) * mm, "end": v(5.42, 9.8) * mm});
            skArc(sketch, "E25.26.6", {"start": v(4.96, 8.62) * mm, "mid": v(4.97, 8.79) * mm, "end": v(5, 8.94) * mm});
            skArc(sketch, "E25.27.0", {"start": v(1.5, 9.84) * mm, "mid": v(1.6, 9.97) * mm, "end": v(1.66, 10.11) * mm});
            skLineSegment(sketch, "E25.27.1", {"start": v(1.66, 10.11) * mm, "end": v(1.88, 11.04) * mm});
            skArc(sketch, "E25.27.2", {"start": v(2.47, 11.95) * mm, "mid": v(2.11, 11.54) * mm, "end": v(1.88, 11.04) * mm});
            skArc(sketch, "E25.27.3", {"start": v(2.96, 11.84) * mm, "mid": v(2.71, 11.9) * mm, "end": v(2.47, 11.95) * mm});
            skArc(sketch, "E25.27.4", {"start": v(2.96, 11.84) * mm, "mid": v(3.1, 11.3) * mm, "end": v(3.1, 10.76) * mm});
            skLineSegment(sketch, "E25.27.5", {"start": v(2.89, 9.83) * mm, "end": v(3.1, 10.76) * mm});
            skArc(sketch, "E25.27.6", {"start": v(2.92, 9.51) * mm, "mid": v(2.9, 9.67) * mm, "end": v(2.89, 9.83) * mm});
            skArc(sketch, "E26", {"start": v(0.73, 9.92) * mm, "mid": v(1.11, 9.89) * mm, "end": v(1.5, 9.84) * mm});
            skArc(sketch, "E27.1.0", {"start": v(-1.5, 9.84) * mm, "mid": v(-1.11, 9.89) * mm, "end": v(-0.73, 9.92) * mm});
            skArc(sketch, "E27.2.0", {"start": v(-3.65, 9.26) * mm, "mid": v(-3.29, 9.4) * mm, "end": v(-2.92, 9.51) * mm});
            skArc(sketch, "E27.3.0", {"start": v(-5.62, 8.21) * mm, "mid": v(-5.3, 8.42) * mm, "end": v(-4.96, 8.62) * mm});
            skArc(sketch, "E27.4.0", {"start": v(-7.3, 6.76) * mm, "mid": v(-7.04, 7.04) * mm, "end": v(-6.76, 7.3) * mm});
            skArc(sketch, "E27.5.0", {"start": v(-8.62, 4.96) * mm, "mid": v(-8.42, 5.3) * mm, "end": v(-8.21, 5.62) * mm});
            skArc(sketch, "E27.6.0", {"start": v(-9.51, 2.92) * mm, "mid": v(-9.4, 3.29) * mm, "end": v(-9.26, 3.65) * mm});
            skArc(sketch, "E27.7.0", {"start": v(-9.92, 0.73) * mm, "mid": v(-9.89, 1.11) * mm, "end": v(-9.84, 1.5) * mm});
            skArc(sketch, "E27.8.0", {"start": v(-9.84, -1.5) * mm, "mid": v(-9.89, -1.11) * mm, "end": v(-9.92, -0.73) * mm});
            skArc(sketch, "E27.9.0", {"start": v(-9.26, -3.65) * mm, "mid": v(-9.4, -3.29) * mm, "end": v(-9.51, -2.92) * mm});
            skArc(sketch, "E27.10.0", {"start": v(-8.21, -5.62) * mm, "mid": v(-8.42, -5.3) * mm, "end": v(-8.62, -4.96) * mm});
            skArc(sketch, "E27.11.0", {"start": v(-6.76, -7.3) * mm, "mid": v(-7.04, -7.04) * mm, "end": v(-7.3, -6.76) * mm});
            skArc(sketch, "E27.12.0", {"start": v(-4.96, -8.62) * mm, "mid": v(-5.3, -8.42) * mm, "end": v(-5.62, -8.21) * mm});
            skArc(sketch, "E27.13.0", {"start": v(-2.92, -9.51) * mm, "mid": v(-3.29, -9.4) * mm, "end": v(-3.65, -9.26) * mm});
            skArc(sketch, "E27.14.0", {"start": v(-0.73, -9.92) * mm, "mid": v(-1.11, -9.89) * mm, "end": v(-1.5, -9.84) * mm});
            skArc(sketch, "E27.15.0", {"start": v(1.5, -9.84) * mm, "mid": v(1.11, -9.89) * mm, "end": v(0.73, -9.92) * mm});
            skArc(sketch, "E27.16.0", {"start": v(3.65, -9.26) * mm, "mid": v(3.29, -9.4) * mm, "end": v(2.92, -9.51) * mm});
            skArc(sketch, "E27.17.0", {"start": v(5.62, -8.21) * mm, "mid": v(5.3, -8.42) * mm, "end": v(4.96, -8.62) * mm});
            skArc(sketch, "E27.18.0", {"start": v(7.3, -6.76) * mm, "mid": v(7.04, -7.04) * mm, "end": v(6.76, -7.3) * mm});
            skArc(sketch, "E27.19.0", {"start": v(8.62, -4.96) * mm, "mid": v(8.42, -5.3) * mm, "end": v(8.21, -5.62) * mm});
            skArc(sketch, "E27.20.0", {"start": v(9.51, -2.92) * mm, "mid": v(9.4, -3.29) * mm, "end": v(9.26, -3.65) * mm});
            skArc(sketch, "E27.21.0", {"start": v(9.92, -0.73) * mm, "mid": v(9.89, -1.11) * mm, "end": v(9.84, -1.5) * mm});
            skArc(sketch, "E27.22.0", {"start": v(9.84, 1.5) * mm, "mid": v(9.89, 1.11) * mm, "end": v(9.92, 0.73) * mm});
            skArc(sketch, "E27.23.0", {"start": v(9.26, 3.65) * mm, "mid": v(9.4, 3.29) * mm, "end": v(9.51, 2.92) * mm});
            skArc(sketch, "E27.24.0", {"start": v(8.21, 5.62) * mm, "mid": v(8.42, 5.3) * mm, "end": v(8.62, 4.96) * mm});
            skArc(sketch, "E27.25.0", {"start": v(6.76, 7.3) * mm, "mid": v(7.04, 7.04) * mm, "end": v(7.3, 6.76) * mm});
            skArc(sketch, "E27.26.0", {"start": v(4.96, 8.62) * mm, "mid": v(5.3, 8.42) * mm, "end": v(5.62, 8.21) * mm});
            skArc(sketch, "E27.27.0", {"start": v(2.92, 9.51) * mm, "mid": v(3.29, 9.4) * mm, "end": v(3.65, 9.26) * mm});
            skSolve(sketch);
        }
        {
            var Q0;
            Q0 = qSketchRegion(id + "F2", true);
            extrude(context, id + "F3", {"entities" : qUnion([Q0]), "operationType" : NewBodyOperationType.ADD, "oppositeDirection" : true, "depth" : 10 * mm, "offsetDistance" : 25 * mm});
        }
    });
